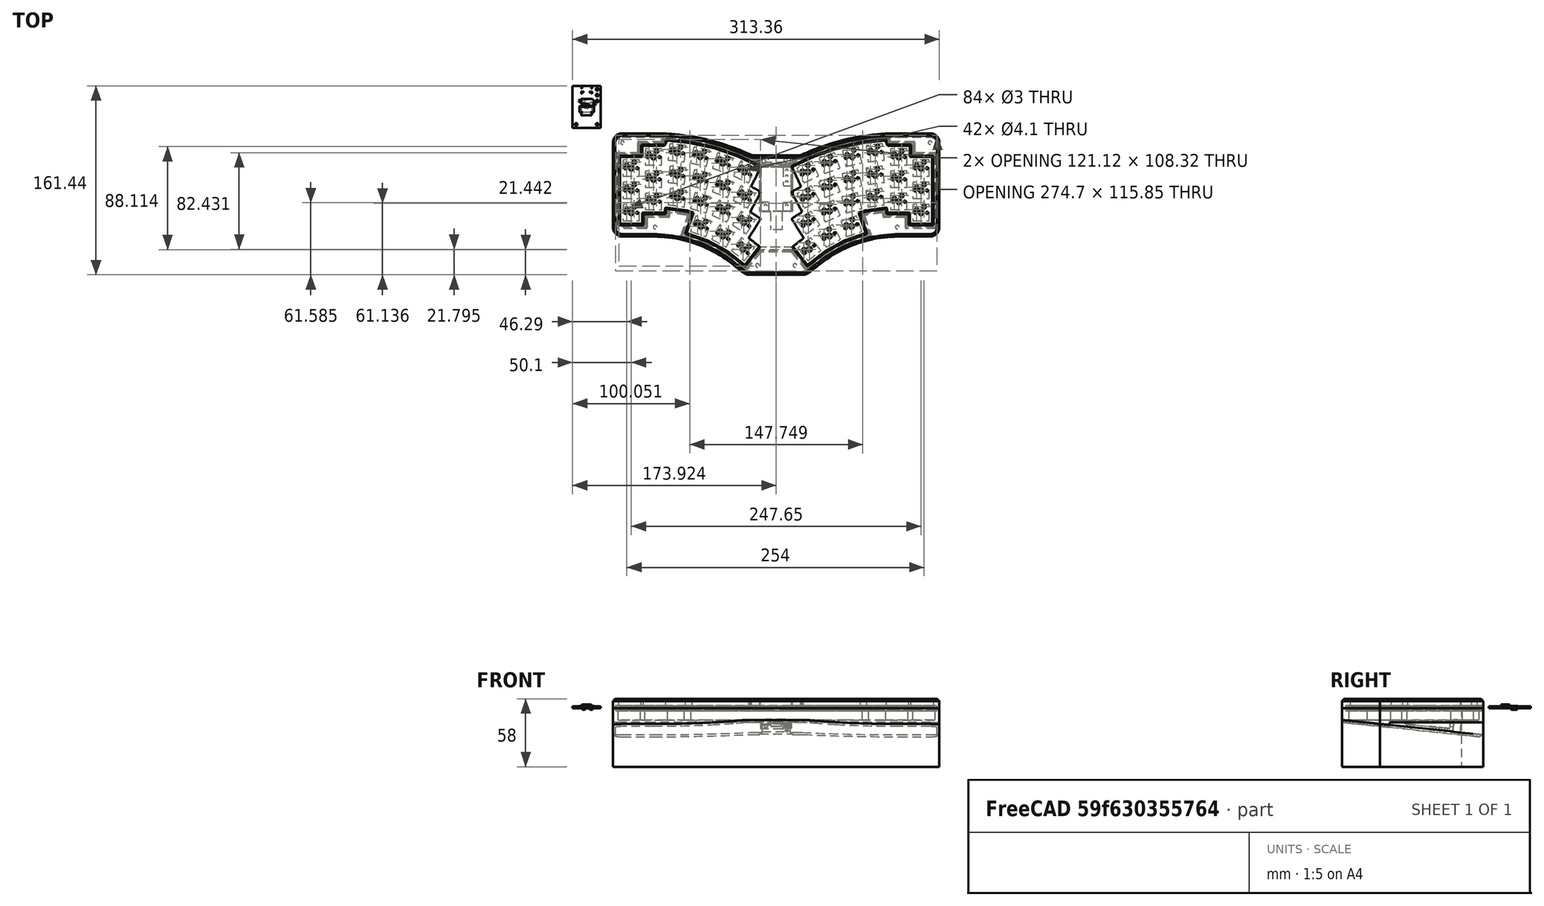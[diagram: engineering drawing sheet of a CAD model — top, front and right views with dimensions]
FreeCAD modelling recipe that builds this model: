
FCSTD DOCUMENT  (FreeCAD 0.21R33771 (Git))
Label: harmony-42-case
License: All rights reserved
LicenseURL: http://en.wikipedia.org/wiki/All_rights_reserved
objects: Part::Feature×116, App::Part×115, Sketcher::SketchObject×16, PartDesign::Pocket×11, PartDesign::Fillet×11, PartDesign::Pad×5, TechDraw::DrawViewBalloon×5, PartDesign::Body×3, PartDesign::Chamfer×3, PartDesign::Boolean×1, PartDesign::Hole×1, TechDraw::DrawSVGTemplate×1, TechDraw::DrawViewPart×1, TechDraw::DrawPage×1, App::DocumentObjectGroup×1
note: 198 computed .brp shape members not serialized (recipe doc carries the construction recipe); baked Part::Feature solids carry a one-line shape summary decoded from their .brp

FEATURE [Sketcher::SketchObject] Sketch
  FullyConstrained = false
  sketch-geometry (14):
    g0: BSplineCurve PolesCount=4 KnotsCount=2 Degree=3 IsPeriodic=0
    g1: BSplineCurve PolesCount=2 KnotsCount=2 Degree=1 IsPeriodic=0
    g2: BSplineCurve PolesCount=2 KnotsCount=2 Degree=1 IsPeriodic=0
    g3: BSplineCurve PolesCount=2 KnotsCount=2 Degree=1 IsPeriodic=0
    g4: BSplineCurve PolesCount=4 KnotsCount=2 Degree=3 IsPeriodic=0
    g5: BSplineCurve PolesCount=2 KnotsCount=2 Degree=1 IsPeriodic=0
    g6: BSplineCurve PolesCount=2 KnotsCount=2 Degree=1 IsPeriodic=0
    g7: BSplineCurve PolesCount=2 KnotsCount=2 Degree=1 IsPeriodic=0
    g8: BSplineCurve PolesCount=4 KnotsCount=2 Degree=3 IsPeriodic=0
    g9: BSplineCurve PolesCount=2 KnotsCount=2 Degree=1 IsPeriodic=0
    g10: BSplineCurve PolesCount=2 KnotsCount=2 Degree=1 IsPeriodic=0
    g11: BSplineCurve PolesCount=2 KnotsCount=2 Degree=1 IsPeriodic=0
    g12: BSplineCurve PolesCount=4 KnotsCount=2 Degree=3 IsPeriodic=0
    g13: BSplineCurve PolesCount=2 KnotsCount=2 Degree=1 IsPeriodic=0
  constraints (14):
    c: Coincident(g0,g1)
    c: Coincident(g1,g2)
    c: Coincident(g2,g3)
    c: Coincident(g3,g4)
    c: Coincident(g4,g5)
    c: Coincident(g5,g6)
    c: Coincident(g6,g7)
    c: Coincident(g7,g8)
    c: Coincident(g8,g9)
    c: Coincident(g9,g10)
    c: Coincident(g10,g11)
    c: Coincident(g11,g12)
    c: Coincident(g12,g13)
    c: Coincident(g13,g0)
FEATURE [PartDesign::Pad] Pad
  Direction = (0,0,1)
  Length = 12
  Length2 = 10
  Profile = -> Sketch
  ReferenceAxis = -> Sketch [N_Axis]
  Reversed = true
  Type = 0
FEATURE [Sketcher::SketchObject] Sketch001
  FullyConstrained = false
  Placement = pos=(0,0,0) rot=(0,0,1;3.14159rad)
  sketch-geometry (42):
    g0: BSplineCurve PolesCount=2 KnotsCount=2 Degree=1 IsPeriodic=0
    g1: BSplineCurve PolesCount=2 KnotsCount=2 Degree=1 IsPeriodic=0
    g2: BSplineCurve PolesCount=2 KnotsCount=2 Degree=1 IsPeriodic=0
    g3: BSplineCurve PolesCount=2 KnotsCount=2 Degree=1 IsPeriodic=0
    g4: BSplineCurve PolesCount=2 KnotsCount=2 Degree=1 IsPeriodic=0
    g5: BSplineCurve PolesCount=2 KnotsCount=2 Degree=1 IsPeriodic=0
    g6: BSplineCurve PolesCount=2 KnotsCount=2 Degree=1 IsPeriodic=0
    g7: BSplineCurve PolesCount=2 KnotsCount=2 Degree=1 IsPeriodic=0
    g8: BSplineCurve PolesCount=2 KnotsCount=2 Degree=1 IsPeriodic=0
    g9: BSplineCurve PolesCount=2 KnotsCount=2 Degree=1 IsPeriodic=0
    g10: BSplineCurve PolesCount=2 KnotsCount=2 Degree=1 IsPeriodic=0
    g11: BSplineCurve PolesCount=2 KnotsCount=2 Degree=1 IsPeriodic=0
    g12: BSplineCurve PolesCount=2 KnotsCount=2 Degree=1 IsPeriodic=0
    g13: BSplineCurve PolesCount=2 KnotsCount=2 Degree=1 IsPeriodic=0
    g14: BSplineCurve PolesCount=2 KnotsCount=2 Degree=1 IsPeriodic=0
    g15: BSplineCurve PolesCount=2 KnotsCount=2 Degree=1 IsPeriodic=0
    g16: BSplineCurve PolesCount=2 KnotsCount=2 Degree=1 IsPeriodic=0
    g17: BSplineCurve PolesCount=2 KnotsCount=2 Degree=1 IsPeriodic=0
    g18: BSplineCurve PolesCount=2 KnotsCount=2 Degree=1 IsPeriodic=0
    g19: BSplineCurve PolesCount=2 KnotsCount=2 Degree=1 IsPeriodic=0
    g20: BSplineCurve PolesCount=2 KnotsCount=2 Degree=1 IsPeriodic=0
    g21: BSplineCurve PolesCount=2 KnotsCount=2 Degree=1 IsPeriodic=0
    g22: BSplineCurve PolesCount=2 KnotsCount=2 Degree=1 IsPeriodic=0
    g23: BSplineCurve PolesCount=2 KnotsCount=2 Degree=1 IsPeriodic=0
    g24: BSplineCurve PolesCount=2 KnotsCount=2 Degree=1 IsPeriodic=0
    g25: BSplineCurve PolesCount=2 KnotsCount=2 Degree=1 IsPeriodic=0
    g26: BSplineCurve PolesCount=2 KnotsCount=2 Degree=1 IsPeriodic=0
    g27: BSplineCurve PolesCount=2 KnotsCount=2 Degree=1 IsPeriodic=0
    g28: BSplineCurve PolesCount=2 KnotsCount=2 Degree=1 IsPeriodic=0
    g29: BSplineCurve PolesCount=2 KnotsCount=2 Degree=1 IsPeriodic=0
    g30: BSplineCurve PolesCount=2 KnotsCount=2 Degree=1 IsPeriodic=0
    g31: BSplineCurve PolesCount=2 KnotsCount=2 Degree=1 IsPeriodic=0
    g32: BSplineCurve PolesCount=2 KnotsCount=2 Degree=1 IsPeriodic=0
    g33: BSplineCurve PolesCount=2 KnotsCount=2 Degree=1 IsPeriodic=0
    g34: BSplineCurve PolesCount=2 KnotsCount=2 Degree=1 IsPeriodic=0
    g35: BSplineCurve PolesCount=2 KnotsCount=2 Degree=1 IsPeriodic=0
    g36: BSplineCurve PolesCount=2 KnotsCount=2 Degree=1 IsPeriodic=0
    g37: BSplineCurve PolesCount=2 KnotsCount=2 Degree=1 IsPeriodic=0
    g38: BSplineCurve PolesCount=2 KnotsCount=2 Degree=1 IsPeriodic=0
    g39: BSplineCurve PolesCount=2 KnotsCount=2 Degree=1 IsPeriodic=0
    g40: BSplineCurve PolesCount=2 KnotsCount=2 Degree=1 IsPeriodic=0
    g41: BSplineCurve PolesCount=2 KnotsCount=2 Degree=1 IsPeriodic=0
  constraints (42):
    c: Coincident(g0,g1)
    c: Coincident(g1,g2)
    c: Coincident(g2,g3)
    c: Coincident(g3,g4)
    c: Coincident(g4,g5)
    c: Coincident(g5,g6)
    c: Coincident(g6,g7)
    c: Coincident(g7,g8)
    c: Coincident(g8,g9)
    c: Coincident(g9,g10)
    c: Coincident(g10,g11)
    c: Coincident(g11,g12)
    c: Coincident(g12,g13)
    c: Coincident(g13,g14)
    c: Coincident(g14,g15)
    c: Coincident(g15,g16)
    c: Coincident(g16,g17)
    c: Coincident(g17,g18)
    c: Coincident(g18,g19)
    c: Coincident(g19,g20)
    c: Coincident(g20,g21)
    c: Coincident(g21,g22)
    c: Coincident(g22,g23)
    c: Coincident(g23,g24)
    c: Coincident(g24,g25)
    c: Coincident(g25,g26)
    c: Coincident(g26,g27)
    c: Coincident(g27,g28)
    c: Coincident(g28,g29)
    c: Coincident(g29,g30)
    c: Coincident(g30,g31)
    c: Coincident(g31,g32)
    c: Coincident(g32,g33)
    c: Coincident(g33,g34)
    c: Coincident(g34,g35)
    c: Coincident(g35,g36)
    c: Coincident(g36,g37)
    c: Coincident(g37,g38)
    c: Coincident(g38,g39)
    c: Coincident(g39,g40)
    c: Coincident(g40,g41)
    c: Coincident(g41,g0)
FEATURE [PartDesign::Pocket] Pocket
  BaseFeature = -> Pad
  Direction = (0,0,-1)
  Length = 10
  Length2 = 5
  Profile = -> Sketch001
  ReferenceAxis = -> Sketch001 [N_Axis]
  Type = 0
FEATURE [Sketcher::SketchObject] Sketch002
  FullyConstrained = false
  Placement = pos=(0,0,0) rot=(0,0,1;3.14159rad)
  sketch-geometry (42):
    g0: BSplineCurve PolesCount=2 KnotsCount=2 Degree=1 IsPeriodic=0
    g1: BSplineCurve PolesCount=2 KnotsCount=2 Degree=1 IsPeriodic=0
    g2: BSplineCurve PolesCount=2 KnotsCount=2 Degree=1 IsPeriodic=0
    g3: BSplineCurve PolesCount=2 KnotsCount=2 Degree=1 IsPeriodic=0
    g4: BSplineCurve PolesCount=2 KnotsCount=2 Degree=1 IsPeriodic=0
    g5: BSplineCurve PolesCount=2 KnotsCount=2 Degree=1 IsPeriodic=0
    g6: BSplineCurve PolesCount=2 KnotsCount=2 Degree=1 IsPeriodic=0
    g7: BSplineCurve PolesCount=2 KnotsCount=2 Degree=1 IsPeriodic=0
    g8: BSplineCurve PolesCount=2 KnotsCount=2 Degree=1 IsPeriodic=0
    g9: BSplineCurve PolesCount=2 KnotsCount=2 Degree=1 IsPeriodic=0
    g10: BSplineCurve PolesCount=2 KnotsCount=2 Degree=1 IsPeriodic=0
    g11: BSplineCurve PolesCount=2 KnotsCount=2 Degree=1 IsPeriodic=0
    g12: BSplineCurve PolesCount=2 KnotsCount=2 Degree=1 IsPeriodic=0
    g13: BSplineCurve PolesCount=2 KnotsCount=2 Degree=1 IsPeriodic=0
    g14: BSplineCurve PolesCount=2 KnotsCount=2 Degree=1 IsPeriodic=0
    g15: BSplineCurve PolesCount=2 KnotsCount=2 Degree=1 IsPeriodic=0
    g16: BSplineCurve PolesCount=2 KnotsCount=2 Degree=1 IsPeriodic=0
    g17: BSplineCurve PolesCount=2 KnotsCount=2 Degree=1 IsPeriodic=0
    g18: BSplineCurve PolesCount=2 KnotsCount=2 Degree=1 IsPeriodic=0
    g19: BSplineCurve PolesCount=2 KnotsCount=2 Degree=1 IsPeriodic=0
    g20: BSplineCurve PolesCount=2 KnotsCount=2 Degree=1 IsPeriodic=0
    g21: BSplineCurve PolesCount=2 KnotsCount=2 Degree=1 IsPeriodic=0
    g22: BSplineCurve PolesCount=2 KnotsCount=2 Degree=1 IsPeriodic=0
    g23: BSplineCurve PolesCount=2 KnotsCount=2 Degree=1 IsPeriodic=0
    g24: BSplineCurve PolesCount=2 KnotsCount=2 Degree=1 IsPeriodic=0
    g25: BSplineCurve PolesCount=2 KnotsCount=2 Degree=1 IsPeriodic=0
    g26: BSplineCurve PolesCount=2 KnotsCount=2 Degree=1 IsPeriodic=0
    g27: BSplineCurve PolesCount=2 KnotsCount=2 Degree=1 IsPeriodic=0
    g28: BSplineCurve PolesCount=2 KnotsCount=2 Degree=1 IsPeriodic=0
    g29: BSplineCurve PolesCount=2 KnotsCount=2 Degree=1 IsPeriodic=0
    g30: BSplineCurve PolesCount=2 KnotsCount=2 Degree=1 IsPeriodic=0
    g31: BSplineCurve PolesCount=2 KnotsCount=2 Degree=1 IsPeriodic=0
    g32: BSplineCurve PolesCount=2 KnotsCount=2 Degree=1 IsPeriodic=0
    g33: BSplineCurve PolesCount=2 KnotsCount=2 Degree=1 IsPeriodic=0
    g34: BSplineCurve PolesCount=2 KnotsCount=2 Degree=1 IsPeriodic=0
    g35: BSplineCurve PolesCount=2 KnotsCount=2 Degree=1 IsPeriodic=0
    g36: BSplineCurve PolesCount=2 KnotsCount=2 Degree=1 IsPeriodic=0
    g37: BSplineCurve PolesCount=2 KnotsCount=2 Degree=1 IsPeriodic=0
    g38: BSplineCurve PolesCount=2 KnotsCount=2 Degree=1 IsPeriodic=0
    g39: BSplineCurve PolesCount=2 KnotsCount=2 Degree=1 IsPeriodic=0
    g40: BSplineCurve PolesCount=2 KnotsCount=2 Degree=1 IsPeriodic=0
    g41: BSplineCurve PolesCount=2 KnotsCount=2 Degree=1 IsPeriodic=0
  constraints (42):
    c: Coincident(g0,g1)
    c: Coincident(g1,g2)
    c: Coincident(g2,g3)
    c: Coincident(g3,g4)
    c: Coincident(g4,g5)
    c: Coincident(g5,g6)
    c: Coincident(g6,g7)
    c: Coincident(g7,g8)
    c: Coincident(g8,g9)
    c: Coincident(g9,g10)
    c: Coincident(g10,g11)
    c: Coincident(g11,g12)
    c: Coincident(g12,g13)
    c: Coincident(g13,g14)
    c: Coincident(g14,g15)
    c: Coincident(g15,g16)
    c: Coincident(g16,g17)
    c: Coincident(g17,g18)
    c: Coincident(g18,g19)
    c: Coincident(g19,g20)
    c: Coincident(g20,g21)
    c: Coincident(g21,g22)
    c: Coincident(g22,g23)
    c: Coincident(g23,g24)
    c: Coincident(g24,g25)
    c: Coincident(g25,g26)
    c: Coincident(g26,g27)
    c: Coincident(g27,g28)
    c: Coincident(g28,g29)
    c: Coincident(g29,g30)
    c: Coincident(g30,g31)
    c: Coincident(g31,g32)
    c: Coincident(g32,g33)
    c: Coincident(g33,g34)
    c: Coincident(g34,g35)
    c: Coincident(g35,g36)
    c: Coincident(g36,g37)
    c: Coincident(g37,g38)
    c: Coincident(g38,g39)
    c: Coincident(g39,g40)
    c: Coincident(g40,g41)
    c: Coincident(g41,g0)
FEATURE [PartDesign::Pocket] Pocket001  label="Pocket001 - Gasket"
  BaseFeature = -> Pocket
  Direction = (0,0,-1)
  Length = 2.25
  Length2 = 5
  Profile = -> Sketch002
  ReferenceAxis = -> Sketch002 [N_Axis]
  Type = 0
  expr: Length = 1.5 mm / 2 + 2 mm - 0.5 mm
FEATURE [Sketcher::SketchObject] Sketch003
  FullyConstrained = false
  sketch-geometry (14):
    g0: BSplineCurve PolesCount=4 KnotsCount=2 Degree=3 IsPeriodic=0
    g1: BSplineCurve PolesCount=2 KnotsCount=2 Degree=1 IsPeriodic=0
    g2: BSplineCurve PolesCount=2 KnotsCount=2 Degree=1 IsPeriodic=0
    g3: BSplineCurve PolesCount=2 KnotsCount=2 Degree=1 IsPeriodic=0
    g4: BSplineCurve PolesCount=4 KnotsCount=2 Degree=3 IsPeriodic=0
    g5: BSplineCurve PolesCount=2 KnotsCount=2 Degree=1 IsPeriodic=0
    g6: BSplineCurve PolesCount=2 KnotsCount=2 Degree=1 IsPeriodic=0
    g7: BSplineCurve PolesCount=2 KnotsCount=2 Degree=1 IsPeriodic=0
    g8: BSplineCurve PolesCount=4 KnotsCount=2 Degree=3 IsPeriodic=0
    g9: BSplineCurve PolesCount=2 KnotsCount=2 Degree=1 IsPeriodic=0
    g10: BSplineCurve PolesCount=2 KnotsCount=2 Degree=1 IsPeriodic=0
    g11: BSplineCurve PolesCount=2 KnotsCount=2 Degree=1 IsPeriodic=0
    g12: BSplineCurve PolesCount=4 KnotsCount=2 Degree=3 IsPeriodic=0
    g13: BSplineCurve PolesCount=2 KnotsCount=2 Degree=1 IsPeriodic=0
  constraints (14):
    c: Coincident(g0,g1)
    c: Coincident(g1,g2)
    c: Coincident(g2,g3)
    c: Coincident(g3,g4)
    c: Coincident(g4,g5)
    c: Coincident(g5,g6)
    c: Coincident(g6,g7)
    c: Coincident(g7,g8)
    c: Coincident(g8,g9)
    c: Coincident(g9,g10)
    c: Coincident(g10,g11)
    c: Coincident(g11,g12)
    c: Coincident(g12,g13)
    c: Coincident(g13,g0)
FEATURE [PartDesign::Pad] Pad001
  Direction = (0,0,1)
  Length = 8
  Length2 = 10
  Profile = -> Sketch003
  ReferenceAxis = -> Sketch003 [N_Axis]
  Type = 0
FEATURE [Sketcher::SketchObject] Sketch004
  FullyConstrained = false
  sketch-geometry (52):
    g0: BSplineCurve PolesCount=2 KnotsCount=2 Degree=1 IsPeriodic=0
    g1: BSplineCurve PolesCount=2 KnotsCount=2 Degree=1 IsPeriodic=0
    g2: BSplineCurve PolesCount=2 KnotsCount=2 Degree=1 IsPeriodic=0
    g3: BSplineCurve PolesCount=2 KnotsCount=2 Degree=1 IsPeriodic=0
    g4: BSplineCurve PolesCount=2 KnotsCount=2 Degree=1 IsPeriodic=0
    g5: BSplineCurve PolesCount=2 KnotsCount=2 Degree=1 IsPeriodic=0
    g6: BSplineCurve PolesCount=2 KnotsCount=2 Degree=1 IsPeriodic=0
    g7: BSplineCurve PolesCount=2 KnotsCount=2 Degree=1 IsPeriodic=0
    g8: BSplineCurve PolesCount=2 KnotsCount=2 Degree=1 IsPeriodic=0
    g9: BSplineCurve PolesCount=2 KnotsCount=2 Degree=1 IsPeriodic=0
    g10: BSplineCurve PolesCount=2 KnotsCount=2 Degree=1 IsPeriodic=0
    g11: BSplineCurve PolesCount=2 KnotsCount=2 Degree=1 IsPeriodic=0
    g12: BSplineCurve PolesCount=2 KnotsCount=2 Degree=1 IsPeriodic=0
    g13: BSplineCurve PolesCount=2 KnotsCount=2 Degree=1 IsPeriodic=0
    g14: BSplineCurve PolesCount=2 KnotsCount=2 Degree=1 IsPeriodic=0
    g15: BSplineCurve PolesCount=2 KnotsCount=2 Degree=1 IsPeriodic=0
    g16: BSplineCurve PolesCount=2 KnotsCount=2 Degree=1 IsPeriodic=0
    g17: BSplineCurve PolesCount=2 KnotsCount=2 Degree=1 IsPeriodic=0
    g18: BSplineCurve PolesCount=2 KnotsCount=2 Degree=1 IsPeriodic=0
    g19: BSplineCurve PolesCount=2 KnotsCount=2 Degree=1 IsPeriodic=0
    g20: BSplineCurve PolesCount=2 KnotsCount=2 Degree=1 IsPeriodic=0
    g21: BSplineCurve PolesCount=2 KnotsCount=2 Degree=1 IsPeriodic=0
    g22: BSplineCurve PolesCount=2 KnotsCount=2 Degree=1 IsPeriodic=0
    g23: BSplineCurve PolesCount=2 KnotsCount=2 Degree=1 IsPeriodic=0
    g24: BSplineCurve PolesCount=2 KnotsCount=2 Degree=1 IsPeriodic=0
    g25: BSplineCurve PolesCount=2 KnotsCount=2 Degree=1 IsPeriodic=0
    g26: BSplineCurve PolesCount=2 KnotsCount=2 Degree=1 IsPeriodic=0
    g27: BSplineCurve PolesCount=2 KnotsCount=2 Degree=1 IsPeriodic=0
    g28: BSplineCurve PolesCount=2 KnotsCount=2 Degree=1 IsPeriodic=0
    g29: BSplineCurve PolesCount=2 KnotsCount=2 Degree=1 IsPeriodic=0
    g30: BSplineCurve PolesCount=2 KnotsCount=2 Degree=1 IsPeriodic=0
    g31: BSplineCurve PolesCount=2 KnotsCount=2 Degree=1 IsPeriodic=0
    g32: BSplineCurve PolesCount=2 KnotsCount=2 Degree=1 IsPeriodic=0
    g33: BSplineCurve PolesCount=2 KnotsCount=2 Degree=1 IsPeriodic=0
    g34: BSplineCurve PolesCount=2 KnotsCount=2 Degree=1 IsPeriodic=0
    g35: BSplineCurve PolesCount=2 KnotsCount=2 Degree=1 IsPeriodic=0
    g36: BSplineCurve PolesCount=2 KnotsCount=2 Degree=1 IsPeriodic=0
    g37: BSplineCurve PolesCount=2 KnotsCount=2 Degree=1 IsPeriodic=0
    g38: BSplineCurve PolesCount=2 KnotsCount=2 Degree=1 IsPeriodic=0
    g39: BSplineCurve PolesCount=2 KnotsCount=2 Degree=1 IsPeriodic=0
    g40: BSplineCurve PolesCount=2 KnotsCount=2 Degree=1 IsPeriodic=0
    g41: BSplineCurve PolesCount=2 KnotsCount=2 Degree=1 IsPeriodic=0
    g42: BSplineCurve PolesCount=2 KnotsCount=2 Degree=1 IsPeriodic=0
    g43: BSplineCurve PolesCount=2 KnotsCount=2 Degree=1 IsPeriodic=0
    g44: BSplineCurve PolesCount=2 KnotsCount=2 Degree=1 IsPeriodic=0
    g45: BSplineCurve PolesCount=2 KnotsCount=2 Degree=1 IsPeriodic=0
    g46: BSplineCurve PolesCount=2 KnotsCount=2 Degree=1 IsPeriodic=0
    g47: BSplineCurve PolesCount=2 KnotsCount=2 Degree=1 IsPeriodic=0
    g48: BSplineCurve PolesCount=2 KnotsCount=2 Degree=1 IsPeriodic=0
    g49: BSplineCurve PolesCount=2 KnotsCount=2 Degree=1 IsPeriodic=0
    g50: BSplineCurve PolesCount=2 KnotsCount=2 Degree=1 IsPeriodic=0
    g51: BSplineCurve PolesCount=2 KnotsCount=2 Degree=1 IsPeriodic=0
  constraints (52):
    c: Coincident(g0,g1)
    c: Coincident(g1,g2)
    c: Coincident(g2,g3)
    c: Coincident(g3,g4)
    c: Coincident(g4,g5)
    c: Coincident(g5,g6)
    c: Coincident(g6,g7)
    c: Coincident(g7,g8)
    c: Coincident(g8,g9)
    c: Coincident(g9,g10)
    c: Coincident(g10,g11)
    c: Coincident(g11,g12)
    c: Coincident(g12,g13)
    c: Coincident(g13,g14)
    c: Coincident(g14,g15)
    c: Coincident(g15,g16)
    c: Coincident(g16,g17)
    c: Coincident(g17,g18)
    c: Coincident(g18,g19)
    c: Coincident(g19,g20)
    c: Coincident(g20,g21)
    c: Coincident(g21,g22)
    c: Coincident(g22,g23)
    c: Coincident(g23,g24)
    c: Coincident(g24,g25)
    c: Coincident(g25,g0)
    c: Coincident(g26,g27)
    c: Coincident(g27,g28)
    c: Coincident(g28,g29)
    c: Coincident(g29,g30)
    c: Coincident(g30,g31)
    c: Coincident(g31,g32)
    c: Coincident(g32,g33)
    c: Coincident(g33,g34)
    c: Coincident(g34,g35)
    c: Coincident(g35,g36)
    c: Coincident(g36,g37)
    c: Coincident(g37,g38)
    c: Coincident(g38,g39)
    c: Coincident(g39,g40)
    c: Coincident(g40,g41)
    c: Coincident(g41,g42)
    c: Coincident(g42,g43)
    c: Coincident(g43,g44)
    c: Coincident(g44,g45)
    c: Coincident(g45,g46)
    c: Coincident(g46,g47)
    c: Coincident(g47,g48)
    c: Coincident(g48,g49)
    c: Coincident(g49,g50)
    c: Coincident(g50,g51)
    c: Coincident(g51,g26)
FEATURE [PartDesign::Pocket] Pocket002
  BaseFeature = -> Pad001
  Direction = (0,0,-1)
  Length = 5
  Length2 = 5
  Profile = -> Sketch004
  ReferenceAxis = -> Sketch004 [N_Axis]
  Reversed = true
  Type = 1
FEATURE [Sketcher::SketchObject] Sketch005
  FullyConstrained = false
  Placement = pos=(0,0,0) rot=(0,0,1;3.14159rad)
  sketch-geometry (42):
    g0: BSplineCurve PolesCount=2 KnotsCount=2 Degree=1 IsPeriodic=0
    g1: BSplineCurve PolesCount=2 KnotsCount=2 Degree=1 IsPeriodic=0
    g2: BSplineCurve PolesCount=2 KnotsCount=2 Degree=1 IsPeriodic=0
    g3: BSplineCurve PolesCount=2 KnotsCount=2 Degree=1 IsPeriodic=0
    g4: BSplineCurve PolesCount=2 KnotsCount=2 Degree=1 IsPeriodic=0
    g5: BSplineCurve PolesCount=2 KnotsCount=2 Degree=1 IsPeriodic=0
    g6: BSplineCurve PolesCount=2 KnotsCount=2 Degree=1 IsPeriodic=0
    g7: BSplineCurve PolesCount=2 KnotsCount=2 Degree=1 IsPeriodic=0
    g8: BSplineCurve PolesCount=2 KnotsCount=2 Degree=1 IsPeriodic=0
    g9: BSplineCurve PolesCount=2 KnotsCount=2 Degree=1 IsPeriodic=0
    g10: BSplineCurve PolesCount=2 KnotsCount=2 Degree=1 IsPeriodic=0
    g11: BSplineCurve PolesCount=2 KnotsCount=2 Degree=1 IsPeriodic=0
    g12: BSplineCurve PolesCount=2 KnotsCount=2 Degree=1 IsPeriodic=0
    g13: BSplineCurve PolesCount=2 KnotsCount=2 Degree=1 IsPeriodic=0
    g14: BSplineCurve PolesCount=2 KnotsCount=2 Degree=1 IsPeriodic=0
    g15: BSplineCurve PolesCount=2 KnotsCount=2 Degree=1 IsPeriodic=0
    g16: BSplineCurve PolesCount=2 KnotsCount=2 Degree=1 IsPeriodic=0
    g17: BSplineCurve PolesCount=2 KnotsCount=2 Degree=1 IsPeriodic=0
    g18: BSplineCurve PolesCount=2 KnotsCount=2 Degree=1 IsPeriodic=0
    g19: BSplineCurve PolesCount=2 KnotsCount=2 Degree=1 IsPeriodic=0
    g20: BSplineCurve PolesCount=2 KnotsCount=2 Degree=1 IsPeriodic=0
    g21: BSplineCurve PolesCount=2 KnotsCount=2 Degree=1 IsPeriodic=0
    g22: BSplineCurve PolesCount=2 KnotsCount=2 Degree=1 IsPeriodic=0
    g23: BSplineCurve PolesCount=2 KnotsCount=2 Degree=1 IsPeriodic=0
    g24: BSplineCurve PolesCount=2 KnotsCount=2 Degree=1 IsPeriodic=0
    g25: BSplineCurve PolesCount=2 KnotsCount=2 Degree=1 IsPeriodic=0
    g26: BSplineCurve PolesCount=2 KnotsCount=2 Degree=1 IsPeriodic=0
    g27: BSplineCurve PolesCount=2 KnotsCount=2 Degree=1 IsPeriodic=0
    g28: BSplineCurve PolesCount=2 KnotsCount=2 Degree=1 IsPeriodic=0
    g29: BSplineCurve PolesCount=2 KnotsCount=2 Degree=1 IsPeriodic=0
    g30: BSplineCurve PolesCount=2 KnotsCount=2 Degree=1 IsPeriodic=0
    g31: BSplineCurve PolesCount=2 KnotsCount=2 Degree=1 IsPeriodic=0
    g32: BSplineCurve PolesCount=2 KnotsCount=2 Degree=1 IsPeriodic=0
    g33: BSplineCurve PolesCount=2 KnotsCount=2 Degree=1 IsPeriodic=0
    g34: BSplineCurve PolesCount=2 KnotsCount=2 Degree=1 IsPeriodic=0
    g35: BSplineCurve PolesCount=2 KnotsCount=2 Degree=1 IsPeriodic=0
    g36: BSplineCurve PolesCount=2 KnotsCount=2 Degree=1 IsPeriodic=0
    g37: BSplineCurve PolesCount=2 KnotsCount=2 Degree=1 IsPeriodic=0
    g38: BSplineCurve PolesCount=2 KnotsCount=2 Degree=1 IsPeriodic=0
    g39: BSplineCurve PolesCount=2 KnotsCount=2 Degree=1 IsPeriodic=0
    g40: BSplineCurve PolesCount=2 KnotsCount=2 Degree=1 IsPeriodic=0
    g41: BSplineCurve PolesCount=2 KnotsCount=2 Degree=1 IsPeriodic=0
  constraints (42):
    c: Coincident(g0,g1)
    c: Coincident(g1,g2)
    c: Coincident(g2,g3)
    c: Coincident(g3,g4)
    c: Coincident(g4,g5)
    c: Coincident(g5,g6)
    c: Coincident(g6,g7)
    c: Coincident(g7,g8)
    c: Coincident(g8,g9)
    c: Coincident(g9,g10)
    c: Coincident(g10,g11)
    c: Coincident(g11,g12)
    c: Coincident(g12,g13)
    c: Coincident(g13,g14)
    c: Coincident(g14,g15)
    c: Coincident(g15,g16)
    c: Coincident(g16,g17)
    c: Coincident(g17,g18)
    c: Coincident(g18,g19)
    c: Coincident(g19,g20)
    c: Coincident(g20,g21)
    c: Coincident(g21,g22)
    c: Coincident(g22,g23)
    c: Coincident(g23,g24)
    c: Coincident(g24,g25)
    c: Coincident(g25,g26)
    c: Coincident(g26,g27)
    c: Coincident(g27,g28)
    c: Coincident(g28,g29)
    c: Coincident(g29,g30)
    c: Coincident(g30,g31)
    c: Coincident(g31,g32)
    c: Coincident(g32,g33)
    c: Coincident(g33,g34)
    c: Coincident(g34,g35)
    c: Coincident(g35,g36)
    c: Coincident(g36,g37)
    c: Coincident(g37,g38)
    c: Coincident(g38,g39)
    c: Coincident(g39,g40)
    c: Coincident(g40,g41)
    c: Coincident(g41,g0)
FEATURE [PartDesign::Pocket] Pocket003  label="Pocket003 - Gasket"
  BaseFeature = -> Pocket002
  Direction = (0,0,-1)
  Length = 2.25
  Length2 = 5
  Profile = -> Sketch005
  ReferenceAxis = -> Sketch005 [N_Axis]
  Reversed = true
  Type = 0
  expr: Length = 1.5 mm / 2 + 2 mm - 0.5 mm
FEATURE [Sketcher::SketchObject] Sketch006
  FullyConstrained = false
  sketch-geometry (14):
    g0: BSplineCurve PolesCount=4 KnotsCount=2 Degree=3 IsPeriodic=0
    g1: BSplineCurve PolesCount=2 KnotsCount=2 Degree=1 IsPeriodic=0
    g2: BSplineCurve PolesCount=2 KnotsCount=2 Degree=1 IsPeriodic=0
    g3: BSplineCurve PolesCount=2 KnotsCount=2 Degree=1 IsPeriodic=0
    g4: BSplineCurve PolesCount=4 KnotsCount=2 Degree=3 IsPeriodic=0
    g5: BSplineCurve PolesCount=2 KnotsCount=2 Degree=1 IsPeriodic=0
    g6: BSplineCurve PolesCount=2 KnotsCount=2 Degree=1 IsPeriodic=0
    g7: BSplineCurve PolesCount=2 KnotsCount=2 Degree=1 IsPeriodic=0
    g8: BSplineCurve PolesCount=4 KnotsCount=2 Degree=3 IsPeriodic=0
    g9: BSplineCurve PolesCount=2 KnotsCount=2 Degree=1 IsPeriodic=0
    g10: BSplineCurve PolesCount=2 KnotsCount=2 Degree=1 IsPeriodic=0
    g11: BSplineCurve PolesCount=2 KnotsCount=2 Degree=1 IsPeriodic=0
    g12: BSplineCurve PolesCount=4 KnotsCount=2 Degree=3 IsPeriodic=0
    g13: BSplineCurve PolesCount=2 KnotsCount=2 Degree=1 IsPeriodic=0
  constraints (14):
    c: Coincident(g0,g1)
    c: Coincident(g1,g2)
    c: Coincident(g2,g3)
    c: Coincident(g3,g4)
    c: Coincident(g4,g5)
    c: Coincident(g5,g6)
    c: Coincident(g6,g7)
    c: Coincident(g7,g8)
    c: Coincident(g8,g9)
    c: Coincident(g9,g10)
    c: Coincident(g10,g11)
    c: Coincident(g11,g12)
    c: Coincident(g12,g13)
    c: Coincident(g13,g0)
FEATURE [PartDesign::Pad] Pad003
  Direction = (0,0,1)
  Length = 50
  Length2 = 10
  Profile = -> Sketch006
  ReferenceAxis = -> Sketch006 [N_Axis]
  Reversed = true
  Type = 0
FEATURE [PartDesign::Fillet] Fillet
  Base = -> Pocket001 [Edge79,Edge84,Edge77,Edge5,Edge1,Edge8,Edge82,Edge76]
  BaseFeature = -> Pocket001
  Radius = 8
  SupportTransform = false
  UseAllEdges = false
FEATURE [PartDesign::Pad] Pad004
  BaseFeature = -> Fillet
  Direction = (0,-0.105104,-1)
  Length = 20
  Length2 = 10
  Profile = -> Fillet [Face5]
  Type = 0
  UseCustomVector = true
  expr: .Direction.y = -0.10510423526
FEATURE [PartDesign::Fillet] Fillet001
  Base = -> Pad004
  BaseFeature = -> Pad004
  Radius = 1
  SupportTransform = false
  UseAllEdges = false
FEATURE [PartDesign::Fillet] Fillet002
  Base = -> Pad003 [Edge20,Edge17,Edge29,Edge32,Edge8,Edge38,Edge1,Edge5]
  BaseFeature = -> Pad003
  Radius = 8
  SupportTransform = false
  UseAllEdges = false
FEATURE [PartDesign::Body] Body002  label="Body"
  Group = -> [Sketch006,Pad003,Fillet002]
  Origin = -> Origin002
  Tip = -> Fillet002
FEATURE [PartDesign::Boolean] Boolean
  BaseFeature = -> Fillet001
  Group = -> [Body002]
  Type = 2
FEATURE [Sketcher::SketchObject] Sketch007
  ExternalGeometry = -> [Boolean]
  FullyConstrained = true
  MapMode = 5
  Placement = pos=(301.359,0,0) rot=(0.57735,0.57735,0.57735;2.0944rad)
  Support = -> [Boolean]
  sketch-geometry (4):
    g0: LineSegment StartX=-143.442 StartY=-12 StartZ=0 EndX=-23.896 EndY=-24.5648 EndZ=0
    g1: LineSegment StartX=-23.896 StartY=-24.5648 StartZ=0 EndX=-24.6775 EndY=-32 EndZ=0
    g2: LineSegment StartX=-24.6775 StartY=-32 StartZ=0 EndX=-143.442 EndY=-32 EndZ=0
    g3: LineSegment StartX=-143.442 StartY=-32 StartZ=0 EndX=-143.442 EndY=-12 EndZ=0
  constraints (10):
    c: Coincident(g0,g-3)
    c: PointOnObject(g0,g-4)
    c: Perpendicular(g-4,g0)
    c: Coincident(g1,g0)
    c: Coincident(g1,g-4)
    c: Coincident(g2,g1)
    c: Horizontal(g2)
    c: Coincident(g3,g2)
    c: Coincident(g3,g0)
    c: Vertical(g3)
FEATURE [PartDesign::Pocket] Pocket004
  BaseFeature = -> Boolean
  Direction = (-1,0,0)
  Length = 5
  Length2 = 5
  Profile = -> Sketch007
  ReferenceAxis = -> Sketch007 [N_Axis]
  Type = 1
FEATURE [PartDesign::Chamfer] Chamfer
  Angle = 45
  Base = -> Pocket004 [Edge203]
  BaseFeature = -> Pocket004
  ChamferType = 0
  FlipDirection = false
  Size = 2
  Size2 = 1
  SupportTransform = false
  UseAllEdges = false
FEATURE [PartDesign::Fillet] Fillet003
  Base = -> Pocket003 [Edge131,Edge136,Edge129,Edge5,Edge1,Edge8,Edge128,Edge134]
  BaseFeature = -> Pocket003
  Radius = 8
  SupportTransform = false
  UseAllEdges = false
FEATURE [PartDesign::Chamfer] Chamfer001
  Angle = 45
  Base = -> Fillet003 [Edge87]
  BaseFeature = -> Fillet003
  ChamferType = 0
  FlipDirection = false
  Size = 2
  Size2 = 4
  SupportTransform = false
  UseAllEdges = false
FEATURE [PartDesign::Fillet] Fillet004
  Base = -> Chamfer001 [Edge232,Edge234,Edge236,Edge238,Edge240,Edge242,Edge244,Edge248,Edge246,Edge250,Edge252,Edge254,Edge256,Edge258,Edge260,Edge262,Edge264,Edge266,Edge268,Edge188,Edge187,Edge190,Edge192,Edge194,Edge196,Edge200,Edge198,Edge202,Edge204,Edge206,Edge208,Edge210,Edge212,Edge214,Edge216,Edge220,Edge222,Edge224,Edge226,Edge228,+2 more]
  BaseFeature = -> Chamfer001
  Radius = 1
  SupportTransform = false
  UseAllEdges = false
FEATURE [PartDesign::Fillet] Fillet005
  Base = -> Fillet004 [Edge480,Edge478,Edge476,Edge474,Edge472,Edge482,Edge484,Edge486,Edge488,Edge490,Edge492,Edge494,Edge496,Edge498,Edge500,Edge502,Edge504,Edge506,Edge508,Edge510,Edge512,Edge514,Edge516,Edge469,Edge467,Edge470,Edge415,Edge417,Edge419,Edge421,Edge423,Edge425,Edge427,Edge431,Edge433,Edge435,Edge437,Edge439,Edge441,Edge443,+12 more]
  BaseFeature = -> Fillet004
  Radius = 1
  SupportTransform = false
  UseAllEdges = false
FEATURE [PartDesign::Fillet] Fillet006
  Base = -> Chamfer [Edge196,Edge198,Edge200,Edge194,Edge192,Edge190,Edge202,Edge204,Edge208,Edge206,Edge210,Edge212,Edge214,Edge216,Edge218,Edge222,Edge220,Edge224,Edge226,Edge228,Edge230,Edge232,Edge234,Edge236,Edge238,Edge240,Edge242,Edge244,Edge246,Edge248,Edge250,Edge252,Edge254,Edge256,Edge258,Edge260,Edge262,Edge264,Edge184,Edge183,+2 more]
  BaseFeature = -> Chamfer
  Radius = 1
  SupportTransform = false
  UseAllEdges = false
FEATURE [PartDesign::Fillet] Fillet007
  Base = -> Fillet006 [Edge427,Edge429,Edge425,Edge423,Edge421,Edge431,Edge433,Edge435,Edge437,Edge439,Edge441,Edge443,Edge445,Edge447,Edge449,Edge451,Edge453,Edge455,Edge457,Edge459,Edge461,Edge463,Edge465,Edge467,Edge469,Edge471,Edge473,Edge475,Edge477,Edge479,Edge481,Edge483,Edge485,Edge487,Edge489,Edge491,Edge493,Edge411,Edge413,Edge417,+2 more]
  BaseFeature = -> Fillet006
  Radius = 1
  SupportTransform = false
  UseAllEdges = false
FEATURE [Sketcher::SketchObject] Sketch008
  AttachmentOffset = pos=(0,0,161.925) rot=(0,0,1;0rad)
  ExternalGeometry = -> [Fillet007]
  FullyConstrained = true
  MapMode = 5
  Placement = pos=(161.925,-3.6e-14,3.6e-14) rot=(0.57735,0.57735,0.57735;2.0944rad)
  Support = -> [YZ_Plane]
  expr: .AttachmentOffset.Base.z = 149.925 mm + 24 mm / 2
  expr: Constraints[8] = 36 mm + 2 mm
  sketch-geometry (6):
    g0: LineSegment StartX=-102.836 StartY=-16.2679 StartZ=0 EndX=-31.845 EndY=-23.7293 EndZ=0
    g1: LineSegment StartX=-50.7153 StartY=-10 StartZ=0 EndX=-51.9363 EndY=-21.6176 EndZ=0
    g2: LineSegment StartX=-51.5182 StartY=-17.6395 StartZ=0 EndX=-89.31 EndY=-13.6675 EndZ=0
    g3: LineSegment StartX=-89.31 StartY=-13.6675 StartZ=0 EndX=-88.9246 EndY=-10 EndZ=0
    g4: LineSegment StartX=-88.9246 StartY=-10 StartZ=0 EndX=-50.7153 EndY=-10 EndZ=0
    g5: LineSegment StartX=-50.7153 StartY=-10 StartZ=0 EndX=-51.5182 EndY=-17.6395 EndZ=0
  constraints (16):
    c: Coincident(g0,g-5)
    c: Coincident(g0,g-5)
    c: Coincident(g1,g-3)
    c: PointOnObject(g1,g0)
    c: Perpendicular(g0,g1)
    c: PointOnObject(g2,g1)
    c: Parallel(g2,g0)
    c: Distance(g2,g1) = 4
    c: Distance(g2) = 38
    c: Coincident(g3,g2)
    c: PointOnObject(g3,g-4)
    c: Perpendicular(g3,g2)
    c: Coincident(g4,g3)
    c: Coincident(g4,g1)
    c: Coincident(g5,g4)
    c: Coincident(g5,g2)
FEATURE [PartDesign::Pocket] Pocket005
  BaseFeature = -> Fillet007
  Direction = (-1,2e-16,-3e-16)
  Length = 13
  Length2 = 13
  Profile = -> Sketch008
  ReferenceAxis = -> Sketch008 [N_Axis]
  Type = 4
  expr: Length = 24 mm / 2 + 1 mm
  expr: Length2 = 24 mm / 2 + 1 mm
FEATURE [Sketcher::SketchObject] Sketch009
  ExternalGeometry = -> [Pocket005]
  FullyConstrained = true
  MapMode = 5
  Placement = pos=(5.7e-15,-2.39663,-22.8024) rot=(-1,0,0;0.10472rad)
  Support = -> [Pocket005]
  sketch-geometry (17):
    g0: LineSegment StartX=149.925 StartY=-49.3922 StartZ=0 EndX=173.925 EndY=-49.3922 EndZ=0
    g1: LineSegment StartX=173.925 StartY=-49.3922 StartZ=0 EndX=173.925 EndY=-85.3922 EndZ=0
    g2: LineSegment StartX=173.925 StartY=-85.3922 StartZ=0 EndX=149.925 EndY=-85.3922 EndZ=0
    g3: LineSegment StartX=149.925 StartY=-85.3922 StartZ=0 EndX=149.925 EndY=-49.3922 EndZ=0
    g4: GeomPoint X=161.925 Y=-49.3922 Z=0
    g5: LineSegment StartX=174.925 StartY=-49.3922 StartZ=0 EndX=167.925 EndY=-49.3922 EndZ=0
    g6: LineSegment StartX=167.925 StartY=-49.3922 StartZ=0 EndX=167.925 EndY=-65.3922 EndZ=0
    g7: LineSegment StartX=167.925 StartY=-65.3922 StartZ=0 EndX=174.925 EndY=-65.3922 EndZ=0
    g8: LineSegment StartX=174.925 StartY=-65.3922 StartZ=0 EndX=174.925 EndY=-49.3922 EndZ=0
    g9: LineSegment StartX=174.925 StartY=-87.3922 StartZ=0 EndX=167.925 EndY=-87.3922 EndZ=0
    g10: LineSegment StartX=167.925 StartY=-87.3922 StartZ=0 EndX=167.925 EndY=-79.3922 EndZ=0
    g11: LineSegment StartX=167.925 StartY=-79.3922 StartZ=0 EndX=174.925 EndY=-79.3922 EndZ=0
    g12: LineSegment StartX=174.925 StartY=-79.3922 StartZ=0 EndX=174.925 EndY=-87.3922 EndZ=0
    g13: LineSegment StartX=148.925 StartY=-87.3922 StartZ=0 EndX=155.925 EndY=-87.3922 EndZ=0
    g14: LineSegment StartX=155.925 StartY=-87.3922 StartZ=0 EndX=155.925 EndY=-79.3922 EndZ=0
    g15: LineSegment StartX=155.925 StartY=-79.3922 StartZ=0 EndX=148.925 EndY=-79.3922 EndZ=0
    g16: LineSegment StartX=148.925 StartY=-79.3922 StartZ=0 EndX=148.925 EndY=-87.3922 EndZ=0
  constraints (45):
    c: Coincident(g0,g1)
    c: Coincident(g1,g2)
    c: Coincident(g2,g3)
    c: Coincident(g3,g0)
    c: Horizontal(g0)
    c: Horizontal(g2)
    c: Vertical(g1)
    c: Vertical(g3)
    c: DistanceX(g0,g0) = 24
    c: DistanceY(g1,g1) = 36
    c: Symmetric(g0,g0,g4)
    c: Symmetric(g-4,g-5,g4)
    c: Coincident(g5,g6)
    c: Coincident(g6,g7)
    c: Coincident(g7,g8)
    c: Coincident(g8,g5)
    c: Horizontal(g5)
    c: Horizontal(g7)
    c: Vertical(g6)
    c: Vertical(g8)
    c: Coincident(g5,g-5)
    c: DistanceX(g5,g0) = 6
    c: DistanceY(g6,g6) = 16
    c: Coincident(g9,g10)
    c: Coincident(g10,g11)
    c: Coincident(g11,g12)
    c: Coincident(g12,g9)
    c: Horizontal(g9)
    c: Horizontal(g11)
    c: Vertical(g10)
    c: Vertical(g12)
    c: Coincident(g9,g-6)
    c: DistanceY(g1,g10) = 6
    c: DistanceX(g10,g1) = 6
    c: Coincident(g13,g14)
    c: Coincident(g14,g15)
    c: Coincident(g15,g16)
    c: Coincident(g16,g13)
    c: Horizontal(g13)
    c: Horizontal(g15)
    c: Vertical(g14)
    c: Vertical(g16)
    c: Coincident(g13,g-6)
    c: DistanceY(g2,g14) = 6
    c: DistanceX(g2,g14) = 6
FEATURE [PartDesign::Pad] Pad005
  BaseFeature = -> Pocket005
  Direction = (-3e-16,0.104528,0.994522)
  Length = 0.4
  Length2 = 10
  Profile = -> Sketch009
  ReferenceAxis = -> Sketch009 [N_Axis]
  Type = 0
FEATURE [PartDesign::Fillet] Fillet008
  Base = -> Pad005 [Edge532,Edge534,Edge600,Edge551,Edge536,Edge538,Edge607,Edge540,Edge545,Edge543,Edge541,Edge610,Edge548]
  BaseFeature = -> Pad005
  Radius = 1
  SupportTransform = false
  UseAllEdges = false
FEATURE [Sketcher::SketchObject] Sketch010
  ExternalGeometry = -> [Fillet008]
  FullyConstrained = false
  MapMode = 5
  Placement = pos=(6.1e-15,-2.35482,-22.4046) rot=(-1,0,0;0.10472rad)
  Support = -> [Fillet008]
  sketch-geometry (9):
    g0: LineSegment StartX=152.925 StartY=-82.3922 StartZ=0 EndX=170.925 EndY=-82.3922 EndZ=0
    g1: LineSegment StartX=170.925 StartY=-82.3922 StartZ=0 EndX=170.925 EndY=-57.3922 EndZ=0
    g2: LineSegment StartX=170.925 StartY=-57.3922 StartZ=0 EndX=152.925 EndY=-57.3922 EndZ=0
    g3: LineSegment StartX=152.925 StartY=-57.3922 StartZ=0 EndX=152.925 EndY=-82.3922 EndZ=0
    g4: Circle CenterX=170.925 CenterY=-57.3922 CenterZ=0 NormalX=0 NormalY=0 NormalZ=1 AngleXU=0 Radius=1.7343
    g5: Circle CenterX=170.925 CenterY=-82.3922 CenterZ=0 NormalX=0 NormalY=0 NormalZ=1 AngleXU=0 Radius=1.55026
    g6: Circle CenterX=152.925 CenterY=-82.3922 CenterZ=0 NormalX=0 NormalY=0 NormalZ=1 AngleXU=0 Radius=1.339
    g7: Circle CenterX=170.925 CenterY=-52.3922 CenterZ=0 NormalX=0 NormalY=0 NormalZ=1 AngleXU=0 Radius=1.85738
    g8: Circle CenterX=170.925 CenterY=-62.3922 CenterZ=0 NormalX=0 NormalY=0 NormalZ=1 AngleXU=0 Radius=1.70469
  constraints (19):
    c: Coincident(g0,g1)
    c: Coincident(g1,g2)
    c: Coincident(g2,g3)
    c: Coincident(g3,g0)
    c: Horizontal(g0)
    c: Horizontal(g2)
    c: Vertical(g1)
    c: Vertical(g3)
    c: DistanceX(g0,g-4) = 3
    c: DistanceY(g0,g-3) = 3
    c: DistanceY(g3,g3) = 25
    c: DistanceX(g0,g0) = 18
    c: Coincident(g4,g1)
    c: Coincident(g5,g0)
    c: Coincident(g6,g3)
    c: PointOnObject(g8,g1)
    c: Vertical(g4,g7)
    c: DistanceY(g8,g4) = 5
    c: DistanceY(g4,g7) = 5
FEATURE [PartDesign::Hole] Hole
  BaseFeature = -> Fillet008
  CustomThreadClearance = 0
  Depth = 2.6
  DepthType = 0
  Diameter = 2.4
  DrillForDepth = false
  DrillPoint = 1
  DrillPointAngle = 118
  HoleCutCountersinkAngle = 90
  HoleCutCustomValues = false
  HoleCutDepth = 0
  HoleCutDiameter = 6.1
  HoleCutType = 0
  ModelThread = false
  Profile = -> Sketch010
  Tapered = false
  TaperedAngle = 90
  ThreadClass = 0
  ThreadDepth = 2.6
  ThreadDepthType = 0
  ThreadDirection = 0
  ThreadFit = 0
  ThreadSize = 6
  ThreadType = 1
  Threaded = false
  UseCustomThreadClearance = false
FEATURE [Sketcher::SketchObject] Sketch011
  ExternalGeometry = -> [Hole]
  FullyConstrained = true
  MapMode = 5
  Placement = pos=(-1.23e-14,-49.1216,5.16289) rot=(1,0,0;1.46608rad)
  Support = -> [Hole]
  expr: Constraints[13] = 8.94 mm + 0.1 mm
  sketch-geometry (15):
    g0: LineSegment StartX=149.925 StartY=-20.928 StartZ=0 EndX=173.925 EndY=-20.928 EndZ=0
    g1: LineSegment StartX=149.925 StartY=-17.668 StartZ=0 EndX=173.925 EndY=-17.668 EndZ=0
    g2: GeomPoint X=161.925 Y=-17.668 Z=0
    g3: LineSegment StartX=158.705 StartY=-17.668 StartZ=0 EndX=165.145 EndY=-17.668 EndZ=0
    g4: LineSegment StartX=166.445 StartY=-18.968 StartZ=0 EndX=166.445 EndY=-19.628 EndZ=0
    g5: LineSegment StartX=165.145 StartY=-20.928 StartZ=0 EndX=158.705 EndY=-20.928 EndZ=0
    g6: LineSegment StartX=157.405 StartY=-19.628 StartZ=0 EndX=157.405 EndY=-18.968 EndZ=0
    g7: ArcOfCircle CenterX=158.705 CenterY=-18.968 CenterZ=0 NormalX=0 NormalY=0 NormalZ=1 AngleXU=0 Radius=1.3 StartAngle=1.5708 EndAngle=3.14159
    g8: GeomPoint X=157.405 Y=-17.668 Z=0
    g9: ArcOfCircle CenterX=158.705 CenterY=-19.628 CenterZ=0 NormalX=0 NormalY=0 NormalZ=1 AngleXU=0 Radius=1.3 StartAngle=3.14159 EndAngle=4.71239
    g10: GeomPoint X=157.405 Y=-20.928 Z=0
    g11: ArcOfCircle CenterX=165.145 CenterY=-19.628 CenterZ=0 NormalX=0 NormalY=0 NormalZ=1 AngleXU=0 Radius=1.3 StartAngle=4.71239 EndAngle=6.28319
    g12: GeomPoint X=166.445 Y=-20.928 Z=0
    g13: ArcOfCircle CenterX=165.145 CenterY=-18.968 CenterZ=0 NormalX=0 NormalY=0 NormalZ=1 AngleXU=0 Radius=1.3 StartAngle=-1.8e-15 EndAngle=1.5708
    g14: GeomPoint X=166.445 Y=-17.668 Z=0
  constraints (36):
    c: PointOnObject(g0,g-4)
    c: PointOnObject(g0,g-5)
    c: Horizontal(g0)
    c: DistanceY(g-5,g0) = 1.6
    c: PointOnObject(g1,g-4)
    c: PointOnObject(g1,g-5)
    c: Horizontal(g1)
    c: DistanceY(g0,g1) = 3.26
    c: Symmetric(g1,g1,g2)
    c: Horizontal(g3)
    c: Horizontal(g5)
    c: Vertical(g4)
    c: Vertical(g6)
    c: DistanceX(g8,g14) = 9.04
    c: Symmetric(g8,g14,g2)
    c: PointOnObject(g10,g0)
    c: PointOnObject(g8,g6)
    c: PointOnObject(g8,g3)
    c: Tangent(g6,g7) = 1.5708
    c: Tangent(g3,g7) = 1.5708
    c: PointOnObject(g10,g6)
    c: PointOnObject(g10,g5)
    c: Tangent(g6,g9) = 1.5708
    c: Tangent(g5,g9) = 1.5708
    c: PointOnObject(g12,g5)
    c: PointOnObject(g12,g4)
    c: Tangent(g5,g11) = 1.5708
    c: Tangent(g4,g11) = 1.5708
    c: PointOnObject(g14,g3)
    c: PointOnObject(g14,g4)
    c: Tangent(g3,g13) = 1.5708
    c: Tangent(g4,g13) = 1.5708
    c: Radius(g7) = 1.3
    c: Equal(g7,g9)
    c: Equal(g7,g13)
    c: Equal(g11,g7)
FEATURE [PartDesign::Pocket] Pocket006
  BaseFeature = -> Hole
  Direction = (2e-16,0.994522,-0.104528)
  Length = 5
  Length2 = 5
  Profile = -> Sketch011
  ReferenceAxis = -> Sketch011 [N_Axis]
  Type = 1
FEATURE [Sketcher::SketchObject] Sketch012
  ExternalGeometry = -> [Pocket006]
  FullyConstrained = true
  MapMode = 5
  Placement = pos=(0.000358914,-39.7006,4.1727) rot=(-3e-06,0.743145,0.669131;3.1416rad)
  Support = -> [Pocket006]
  sketch-geometry (9):
    g0: LineSegment StartX=-173.925 StartY=-14.298 StartZ=0 EndX=-149.925 EndY=-14.298 EndZ=0
    g1: LineSegment StartX=-149.925 StartY=-14.298 StartZ=0 EndX=-149.925 EndY=-24.298 EndZ=0
    g2: LineSegment StartX=-149.925 StartY=-24.298 StartZ=0 EndX=-173.925 EndY=-24.298 EndZ=0
    g3: LineSegment StartX=-173.925 StartY=-24.298 StartZ=0 EndX=-173.925 EndY=-14.298 EndZ=0
    g4: GeomPoint X=-161.925 Y=-19.298 Z=0
    g5: LineSegment StartX=-173.925 StartY=-14.298 StartZ=0 EndX=-149.925 EndY=-14.298 EndZ=0
    g6: LineSegment StartX=-149.925 StartY=-14.298 StartZ=0 EndX=-149.925 EndY=-26.928 EndZ=0
    g7: LineSegment StartX=-149.925 StartY=-26.928 StartZ=0 EndX=-173.925 EndY=-26.928 EndZ=0
    g8: LineSegment StartX=-173.925 StartY=-26.928 StartZ=0 EndX=-173.925 EndY=-14.298 EndZ=0
  constraints (23):
    c: Coincident(g0,g1)
    c: Coincident(g1,g2)
    c: Coincident(g2,g3)
    c: Coincident(g3,g0)
    c: Horizontal(g0)
    c: Horizontal(g2)
    c: Vertical(g1)
    c: Vertical(g3)
    c: Symmetric(g-3,g-4,g4)
    c: DistanceX(g0,g0) = 24
    c: DistanceY(g3,g3) = 10
    c: Coincident(g5,g6)
    c: Coincident(g6,g7)
    c: Coincident(g7,g8)
    c: Coincident(g8,g5)
    c: Horizontal(g5)
    c: Horizontal(g7)
    c: Vertical(g6)
    c: Vertical(g8)
    c: Symmetric(g0,g1,g4)
    c: Coincident(g0,g5)
    c: PointOnObject(g6,g-5)
    c: Vertical(g1,g6)
FEATURE [PartDesign::Pocket] Pocket007
  BaseFeature = -> Pocket006
  Direction = (8.99101e-06,-0.994522,0.104528)
  Length = 6.47
  Length2 = 5
  Profile = -> Sketch012
  ReferenceAxis = -> Sketch012 [N_Axis]
  Type = 0
FEATURE [PartDesign::Fillet] Fillet009
  Base = -> Pocket007 [Edge641,Edge640]
  BaseFeature = -> Pocket007
  Radius = 4
  SupportTransform = false
  UseAllEdges = false
FEATURE [PartDesign::Chamfer] Chamfer002
  Angle = 45
  Base = -> Fillet009 [Edge6,Edge26,Edge29]
  BaseFeature = -> Fillet009
  ChamferType = 0
  FlipDirection = false
  Size = 2
  Size2 = 1
  SupportTransform = false
  UseAllEdges = false
FEATURE [Sketcher::SketchObject] Sketch013
  ExternalGeometry = -> [Chamfer002]
  FullyConstrained = true
  MapMode = 5
  Support = -> [Chamfer002]
  sketch-geometry (10):
    g0: Circle CenterX=30.491 CenterY=-30.576 CenterZ=0 NormalX=0 NormalY=0 NormalZ=1 AngleXU=0 Radius=1.5
    g1: Circle CenterX=153.925 CenterY=-45.3989 CenterZ=0 NormalX=0 NormalY=0 NormalZ=1 AngleXU=0 Radius=1.5
    g2: Circle CenterX=293.359 CenterY=-30.5756 CenterZ=0 NormalX=0 NormalY=0 NormalZ=1 AngleXU=0 Radius=1.5
    g3: Circle CenterX=58.491 CenterY=-102.775 CenterZ=0 NormalX=0 NormalY=0 NormalZ=1 AngleXU=0 Radius=1.5
    g4: Circle CenterX=169.925 CenterY=-45.3989 CenterZ=0 NormalX=0 NormalY=0 NormalZ=1 AngleXU=0 Radius=1.5
    g5: Circle CenterX=265.359 CenterY=-102.775 CenterZ=0 NormalX=0 NormalY=0 NormalZ=1 AngleXU=0 Radius=1.5
    g6: GeomPoint X=161.925 Y=-41.3989 Z=0
    g7: GeomPoint X=161.925 Y=-143.442 Z=0
    g8: Circle CenterX=145.925 CenterY=-135.442 CenterZ=0 NormalX=0 NormalY=0 NormalZ=1 AngleXU=0 Radius=1.5
    g9: Circle CenterX=177.925 CenterY=-135.442 CenterZ=0 NormalX=0 NormalY=0 NormalZ=1 AngleXU=0 Radius=1.5
  constraints (26):
    c: Diameter(g0) = 3
    c: Symmetric(g-7,g-7,g6)
    c: DistanceX(g1,g6) = 8
    c: DistanceX(g6,g4) = 8
    c: DistanceY(g1,g6) = 4
    c: Horizontal(g1,g4)
    c: Diameter(g1) = 3
    c: Equal(g1,g4)
    c: DistanceY(g0,g-3) = 8
    c: DistanceX(g-4,g0) = 8
    c: DistanceY(g-5,g3) = 8
    c: Equal(g0,g3)
    c: Symmetric(g-6,g-6,g7)
    c: DistanceX(g8,g7) = 16
    c: DistanceX(g7,g9) = 16
    c: DistanceY(g7,g8) = 8
    c: Horizontal(g8,g9)
    c: Diameter(g8) = 3
    c: Equal(g8,g9)
    c: Equal(g2,g0)
    c: DistanceY(g2,g-10) = 8
    c: DistanceX(g2,g-9) = 8
    c: DistanceX(g-4,g3) = 36
    c: Equal(g3,g5)
    c: DistanceY(g-8,g5) = 8
    c: DistanceX(g5,g-9) = 36
FEATURE [PartDesign::Pocket] Pocket008  label="Pocket008 - Magnet"
  BaseFeature = -> Chamfer002
  Direction = (0,0,-1)
  Length = 1.6
  Length2 = 5
  Profile = -> Sketch013
  ReferenceAxis = -> Sketch013 [N_Axis]
  Type = 0
FEATURE [Sketcher::SketchObject] Sketch014
  ExternalGeometry = -> [Fillet005]
  FullyConstrained = true
  MapMode = 5
  Placement = pos=(0,0,0) rot=(1,0,0;3.14159rad)
  Support = -> [Fillet005]
  sketch-geometry (10):
    g0: Circle CenterX=30.491 CenterY=30.576 CenterZ=0 NormalX=0 NormalY=0 NormalZ=1 AngleXU=0 Radius=1.5
    g1: Circle CenterX=293.359 CenterY=30.5756 CenterZ=0 NormalX=0 NormalY=0 NormalZ=1 AngleXU=0 Radius=1.5
    g2: Circle CenterX=265.359 CenterY=102.775 CenterZ=0 NormalX=0 NormalY=0 NormalZ=1 AngleXU=0 Radius=1.5
    g3: Circle CenterX=58.491 CenterY=102.775 CenterZ=0 NormalX=0 NormalY=0 NormalZ=1 AngleXU=0 Radius=1.5
    g4: Circle CenterX=145.925 CenterY=135.442 CenterZ=0 NormalX=0 NormalY=0 NormalZ=1 AngleXU=0 Radius=1.5
    g5: Circle CenterX=177.925 CenterY=135.442 CenterZ=0 NormalX=0 NormalY=0 NormalZ=1 AngleXU=0 Radius=1.5
    g6: Circle CenterX=153.925 CenterY=45.3989 CenterZ=0 NormalX=0 NormalY=0 NormalZ=1 AngleXU=0 Radius=1.5
    g7: Circle CenterX=169.925 CenterY=45.3989 CenterZ=0 NormalX=0 NormalY=0 NormalZ=1 AngleXU=0 Radius=1.5
    g8: GeomPoint X=161.925 Y=143.442 Z=0
    g9: GeomPoint X=161.925 Y=41.3989 Z=0
  constraints (26):
    c: DistanceY(g-10,g0) = 8
    c: DistanceX(g-3,g0) = 8
    c: Diameter(g0) = 3
    c: DistanceX(g-3,g3) = 36
    c: DistanceY(g3,g-9) = 8
    c: Equal(g0,g3)
    c: Equal(g0,g1)
    c: Equal(g0,g2)
    c: DistanceY(g2,g-8) = 8
    c: DistanceX(g2,g-6) = 36
    c: DistanceX(g1,g-6) = 8
    c: DistanceY(g-7,g1) = 8
    c: Symmetric(g-4,g-4,g9)
    c: Symmetric(g-5,g-5,g8)
    c: DistanceY(g9,g6) = 4
    c: DistanceX(g6,g9) = 8
    c: DistanceX(g9,g7) = 8
    c: Diameter(g6) = 3
    c: Equal(g6,g7)
    c: Horizontal(g6,g7)
    c: Horizontal(g4,g5)
    c: DistanceY(g4,g8) = 8
    c: DistanceX(g4,g8) = 16
    c: DistanceX(g8,g5) = 16
    c: Diameter(g4) = 3
    c: Equal(g4,g5)
FEATURE [PartDesign::Pocket] Pocket009  label="Pocket009 - Magnet"
  BaseFeature = -> Fillet005
  Direction = (0,0,1)
  Length = 1.6
  Length2 = 5
  Profile = -> Sketch014
  ReferenceAxis = -> Sketch014 [N_Axis]
  Type = 0
FEATURE [PartDesign::Body] Body001  label="Top"
  Group = -> [Sketch003,Pad001,Sketch004,Pocket002,Sketch005,Pocket003,Fillet003,Chamfer001,Fillet004,Fillet005,Sketch014,Pocket009]
  Origin = -> Origin001
  Tip = -> Pocket009
FEATURE [Sketcher::SketchObject] Sketch015
  AttachmentOffset = pos=(0,0,161.925) rot=(0,0,1;0rad)
  ExternalGeometry = -> [Pocket008]
  FullyConstrained = true
  MapMode = 5
  Placement = pos=(161.925,-3.6e-14,3.6e-14) rot=(0.57735,0.57735,0.57735;2.0944rad)
  Support = -> [YZ_Plane]
  expr: .AttachmentOffset.Base.z = 149.925 mm + 24 mm / 2
  sketch-geometry (3):
    g0: LineSegment StartX=-88.9246 StartY=-10 StartZ=0 EndX=-105.07 EndY=-10 EndZ=0
    g1: LineSegment StartX=-89.101 StartY=-11.6784 StartZ=0 EndX=-105.07 EndY=-10 EndZ=0
    g2: LineSegment StartX=-88.9246 StartY=-10 StartZ=0 EndX=-89.101 EndY=-11.6784 EndZ=0
  constraints (8):
    c: Coincident(g0,g-4)
    c: Parallel(g-5,g0)
    c: PointOnObject(g1,g-4)
    c: Parallel(g-3,g1)
    c: Distance(g-4,g1) = 1.6
    c: Coincident(g1,g0)
    c: Coincident(g2,g0)
    c: Coincident(g2,g1)
FEATURE [PartDesign::Pocket] Pocket010
  BaseFeature = -> Pocket008
  Direction = (-1,2e-16,-3e-16)
  Length = 5
  Length2 = 5
  Profile = -> Sketch015
  ReferenceAxis = -> Sketch015 [N_Axis]
  Type = 4
FEATURE [PartDesign::Fillet] Fillet010
  Base = -> Pocket010 [Edge808,Edge806]
  BaseFeature = -> Pocket010
  Radius = 1
  SupportTransform = false
  UseAllEdges = false
FEATURE [PartDesign::Body] Body  label="Bottom"
  Group = -> [Sketch,Pad,Sketch001,Pocket,Sketch002,Pocket001,Fillet,Pad004,Fillet001,Boolean,Sketch007,Pocket004,Chamfer,Fillet006,Fillet007,Sketch008,Pocket005,Sketch009,Pad005,Fillet008,Sketch010,Hole,Sketch011,Pocket006,Sketch012,Pocket007,Fillet009,Chamfer002,Sketch013,Pocket008,Sketch015,Pocket010,Fillet010]
  Origin = -> Origin
  Tip = -> Fillet010
FEATURE [Part::Feature] Part__Feature115  label="C_0402_1005Metric032"
  shape: bbox 1 x 0.5 x 0.5 mm, 28 faces (baked)
FEATURE [App::Part] C_0402_1005Metric016  label="C_0402_1005Metric033"
  Group = -> [Part__Feature115]
  Origin = -> Origin118
  Placement = pos=(4.22,6.655,1.65) rot=(0,0,1;1.5708rad)
FEATURE [Part::Feature] Part__Feature116  label="R_0402_1005Metric016"
  shape: bbox 1 x 0.5 x 0.35 mm, 26 faces (baked)
FEATURE [App::Part] R_0402_1005Metric008  label="R_0402_1005Metric017"
  Group = -> [Part__Feature116]
  Origin = -> Origin119
  Placement = pos=(-5.555,2.94,1.65) rot=(0,0,-1;1.5708rad)
FEATURE [Part::Feature] Part__Feature117  label="R_0402_1005Metric018"
  shape: bbox 1 x 0.5 x 0.35 mm, 26 faces (baked)
FEATURE [App::Part] R_0402_1005Metric009  label="R_0402_1005Metric019"
  Group = -> [Part__Feature117]
  Origin = -> Origin120
  Placement = pos=(2.22,6.655,1.65) rot=(0,0,1;1.5708rad)
FEATURE [Part::Feature] Part__Feature118  label="C_0402_1005Metric034"
  shape: bbox 1 x 0.5 x 0.5 mm, 28 faces (baked)
FEATURE [App::Part] C_0402_1005Metric017  label="C_0402_1005Metric035"
  Group = -> [Part__Feature118]
  Origin = -> Origin121
  Placement = pos=(1.58,-5.055,1.65) rot=(0,0,-1;1.5708rad)
FEATURE [Part::Feature] Part__Feature119  label="R_0402_1005Metric020"
  shape: bbox 1 x 0.5 x 0.35 mm, 26 faces (baked)
FEATURE [App::Part] R_0402_1005Metric010  label="R_0402_1005Metric021"
  Group = -> [Part__Feature119]
  Origin = -> Origin122
  Placement = pos=(-0.42,-5.595,1.65) rot=(0,0,-1;1.5708rad)
FEATURE [Part::Feature] Part__Feature120  label="C_0402_1005Metric036"
  shape: bbox 1 x 0.5 x 0.5 mm, 28 faces (baked)
FEATURE [App::Part] C_0402_1005Metric018  label="C_0402_1005Metric037"
  Group = -> [Part__Feature120]
  Origin = -> Origin123
  Placement = pos=(-6.16,-3.385,1.65) rot=(0,0,1;3.14159rad)
FEATURE [Part::Feature] Part__Feature121  label="R_0402_1005Metric022"
  shape: bbox 1 x 0.5 x 0.35 mm, 26 faces (baked)
FEATURE [App::Part] R_0402_1005Metric011  label="R_0402_1005Metric023"
  Group = -> [Part__Feature121]
  Origin = -> Origin124
  Placement = pos=(-10.48,10.285,1.65) rot=(0,0,1;3.14159rad)
FEATURE [Part::Feature] Part__Feature122  label="C_0402_1005Metric038"
  shape: bbox 1 x 0.5 x 0.5 mm, 28 faces (baked)
FEATURE [App::Part] C_0402_1005Metric019  label="C_0402_1005Metric039"
  Group = -> [Part__Feature122]
  Origin = -> Origin125
  Placement = pos=(-7.325,14.895,1.65) rot=(0,0,1;3.14159rad)
FEATURE [Part::Feature] Part__Feature123  label="R_0402_1005Metric024"
  shape: bbox 1 x 0.5 x 0.35 mm, 26 faces (baked)
FEATURE [App::Part] R_0402_1005Metric012  label="R_0402_1005Metric025"
  Group = -> [Part__Feature123]
  Origin = -> Origin126
  Placement = pos=(2.58,-5.055,1.65) rot=(0,0,1;1.5708rad)
FEATURE [Part::Feature] Part__Feature124  label="Crystal_SMD_3225-4Pin_3.2x2.5mm002"
  shape: bbox 3.2 x 2.501 x 0.64 mm, 28 faces (baked)
FEATURE [App::Part] Crystal_SMD_3225_4Pin_3_2x2_5mm001  label="Crystal_SMD_3225-4Pin_3.2x2.5mm003"
  Group = -> [Part__Feature124]
  Origin = -> Origin127
  Placement = pos=(-3.1,-4.925,1.65) rot=(0,0,1;0rad)
FEATURE [Part::Feature] Part__Feature125  label="C_0402_1005Metric040"
  shape: bbox 1 x 0.5 x 0.5 mm, 28 faces (baked)
FEATURE [App::Part] C_0402_1005Metric020  label="C_0402_1005Metric041"
  Group = -> [Part__Feature125]
  Origin = -> Origin128
  Placement = pos=(-1.8,7.94627,1.65) rot=(0,0,1;1.5708rad)
FEATURE [Part::Feature] Part__Feature126  label="C_0402_1005Metric042"
  shape: bbox 1 x 0.5 x 0.5 mm, 28 faces (baked)
FEATURE [App::Part] C_0402_1005Metric021  label="C_0402_1005Metric043"
  Group = -> [Part__Feature126]
  Origin = -> Origin129
  Placement = pos=(-5.64,11.345,1.65) rot=(0,0,1;1.5708rad)
FEATURE [Part::Feature] Part__Feature127  label="C_0402_1005Metric044"
  shape: bbox 1 x 0.5 x 0.5 mm, 28 faces (baked)
FEATURE [App::Part] C_0402_1005Metric022  label="C_0402_1005Metric045"
  Group = -> [Part__Feature127]
  Origin = -> Origin130
  Placement = pos=(-0.8,7.94627,1.65) rot=(0,0,1;1.5708rad)
FEATURE [Part::Feature] Part__Feature128  label="Body004"
  shape: bbox 8.94 x 7.3 x 3.2 mm, 10 faces (baked)
FEATURE [App::Part] HRO_TYPE_C_31_M_12_Body001  label="HRO_TYPE-C-31-M-12-Body001"
  Group = -> [Part__Feature128]
  Origin = -> Origin131
  Placement = pos=(-3e-16,11.705,1.65) rot=(0,0,1;3.14159rad)
FEATURE [Part::Feature] Part__Feature129  label="C_0402_1005Metric046"
  shape: bbox 1 x 0.5 x 0.5 mm, 28 faces (baked)
FEATURE [App::Part] C_0402_1005Metric023  label="C_0402_1005Metric047"
  Group = -> [Part__Feature129]
  Origin = -> Origin132
  Placement = pos=(5.035,3.81,1.65) rot=(0,0,1;0rad)
FEATURE [Part::Feature] Part__Feature130  label="Body005"
  shape: bbox 12.4 x 5.4 x 2 mm, 6 faces (baked)
FEATURE [App::Part] JUSHUO_AFC01_S16FCC_00_Body002  label="JUSHUO_AFC01-S16FCC-00-Body002"
  Group = -> [Part__Feature130]
  Origin = -> Origin133
  Placement = pos=(0,-13.515,1.65) rot=(0,0,1;0rad)
FEATURE [Part::Feature] Part__Feature131  label="C_0402_1005Metric048"
  shape: bbox 1 x 0.5 x 0.5 mm, 28 faces (baked)
FEATURE [App::Part] C_0402_1005Metric024  label="C_0402_1005Metric049"
  Group = -> [Part__Feature131]
  Origin = -> Origin134
  Placement = pos=(5.985,-2.20726,1.65) rot=(0,0,-1;1.5708rad)
FEATURE [Part::Feature] Part__Feature132  label="C_0402_1005Metric050"
  shape: bbox 1 x 0.5 x 0.5 mm, 28 faces (baked)
FEATURE [App::Part] C_0402_1005Metric025  label="C_0402_1005Metric051"
  Group = -> [Part__Feature132]
  Origin = -> Origin135
  Placement = pos=(3.22,6.655,1.65) rot=(0,0,1;1.5708rad)
FEATURE [Part::Feature] Part__Feature133  label="C_0402_1005Metric052"
  shape: bbox 1 x 0.5 x 0.5 mm, 28 faces (baked)
FEATURE [App::Part] C_0402_1005Metric026  label="C_0402_1005Metric053"
  Group = -> [Part__Feature133]
  Origin = -> Origin136
  Placement = pos=(-4.555,2.94,1.65) rot=(0,0,-1;1.5708rad)
FEATURE [Part::Feature] Part__Feature134  label="R_0402_1005Metric026"
  shape: bbox 1 x 0.5 x 0.35 mm, 26 faces (baked)
FEATURE [App::Part] R_0402_1005Metric013  label="R_0402_1005Metric027"
  Group = -> [Part__Feature134]
  Origin = -> Origin137
  Placement = pos=(-2.74,9.865,1.65) rot=(0,0,1;3.14159rad)
FEATURE [Part::Feature] Part__Feature135  label="C_0402_1005Metric054"
  shape: bbox 1 x 0.5 x 0.5 mm, 28 faces (baked)
FEATURE [App::Part] C_0402_1005Metric027  label="C_0402_1005Metric055"
  Group = -> [Part__Feature135]
  Origin = -> Origin138
  Placement = pos=(0.58,-5.055,1.65) rot=(0,0,-1;1.5708rad)
FEATURE [Part::Feature] Part__Feature136  label="C_0402_1005Metric056"
  shape: bbox 1 x 0.5 x 0.5 mm, 28 faces (baked)
FEATURE [App::Part] C_0402_1005Metric028  label="C_0402_1005Metric057"
  Group = -> [Part__Feature136]
  Origin = -> Origin139
  Placement = pos=(0.2,7.94627,1.65) rot=(0,0,1;1.5708rad)
FEATURE [Part::Feature] Part__Feature137  label="C_0402_1005Metric058"
  shape: bbox 1 x 0.5 x 0.5 mm, 28 faces (baked)
FEATURE [App::Part] C_0402_1005Metric029  label="C_0402_1005Metric059"
  Group = -> [Part__Feature137]
  Origin = -> Origin140
  Placement = pos=(5.035,4.81,1.65) rot=(0,0,1;0rad)
FEATURE [Part::Feature] Part__Feature138  label="R_0402_1005Metric028"
  shape: bbox 1 x 0.5 x 0.35 mm, 26 faces (baked)
FEATURE [App::Part] R_0402_1005Metric014  label="R_0402_1005Metric029"
  Group = -> [Part__Feature138]
  Origin = -> Origin141
  Placement = pos=(1.22,6.655,1.65) rot=(0,0,1;1.5708rad)
FEATURE [Part::Feature] Part__Feature139  label="C_0402_1005Metric060"
  shape: bbox 1 x 0.5 x 0.5 mm, 28 faces (baked)
FEATURE [App::Part] C_0402_1005Metric030  label="C_0402_1005Metric061"
  Group = -> [Part__Feature139]
  Origin = -> Origin142
  Placement = pos=(-6.16,-5.775,1.65) rot=(0,0,1;3.14159rad)
FEATURE [Part::Feature] Part__Feature140  label="R_0402_1005Metric030"
  shape: bbox 1 x 0.5 x 0.35 mm, 26 faces (baked)
FEATURE [App::Part] R_0402_1005Metric015  label="R_0402_1005Metric031"
  Group = -> [Part__Feature140]
  Origin = -> Origin143
  Placement = pos=(2.74,9.865,1.65) rot=(0,0,1;0rad)
FEATURE [Part::Feature] Part__Feature141  label="C_0402_1005Metric062"
  shape: bbox 1 x 0.5 x 0.5 mm, 28 faces (baked)
FEATURE [App::Part] C_0402_1005Metric031  label="C_0402_1005Metric063"
  Group = -> [Part__Feature141]
  Origin = -> Origin144
  Placement = pos=(-4.555,0.62,1.65) rot=(0,0,1;1.5708rad)
FEATURE [Part::Feature] Part__Feature142  label="SOT_23_006"
  shape: bbox 2.8 x 2.9 x 1.55 mm, 109 faces (baked)
FEATURE [App::Part] SOT_23_006  label="SOT-23-006"
  Group = -> [Part__Feature142]
  Origin = -> Origin145
  Placement = pos=(-7.8,12.385,1.65) rot=(0,0,1;1.5708rad)
FEATURE [Part::Feature] Part__Feature143  label="mcu-16-pcb_PCB001"
  shape: bbox 24 x 36 x 1.6 mm, 38 faces (baked)
FEATURE [App::Part] mcu_16_pcb_002  label="mcu-16-pcb"
  Group = -> [C_0402_1005Metric016,R_0402_1005Metric008,R_0402_1005Metric009,C_0402_1005Metric017,R_0402_1005Metric010,C_0402_1005Metric018,R_0402_1005Metric011,C_0402_1005Metric019,R_0402_1005Metric012,Crystal_SMD_3225_4Pin_3_2x2_5mm001,C_0402_1005Metric020,C_0402_1005Metric021,C_0402_1005Metric022,HRO_TYPE_C_31_M_12_Body001,C_0402_1005Metric023,JUSHUO_AFC01_S16FCC_00_Body002,C_0402_1005Metric024,+12 more]
  Origin = -> Origin146
  Placement = pos=(161.93,-69.4,-15.35) rot=(-1,0,0;0.10472rad)
FEATURE [Part::Feature] Part__Feature144  label="Hot_Swap_Socket_CPG151101S095"
  shape: bbox 14.5 x 6.096 x 3.05 mm, 90 faces, 3 solids (baked)
FEATURE [App::Part] Hot_Swap_Socket_CPG151101S053  label="Hot_Swap_Socket_CPG151101S096"
  Group = -> [Part__Feature144]
  Origin = -> Origin147
  Placement = pos=(266.7,-42.8625,-0.05) rot=(0,1,0;3.14159rad)
FEATURE [Part::Feature] Part__Feature145  label="Hot_Swap_Socket_CPG151101S097"
  shape: bbox 14.5 x 6.096 x 3.05 mm, 90 faces, 3 solids (baked)
FEATURE [App::Part] Hot_Swap_Socket_CPG151101S054  label="Hot_Swap_Socket_CPG151101S098"
  Group = -> [Part__Feature145]
  Origin = -> Origin148
  Placement = pos=(190.28,-121.645,-0.05) rot=(-0.326467,0.945208,0;3.14159rad)
FEATURE [Part::Feature] Part__Feature146  label="Hot_Swap_Socket_CPG151101S099"
  shape: bbox 14.5 x 6.096 x 3.05 mm, 90 faces, 3 solids (baked)
FEATURE [App::Part] Hot_Swap_Socket_CPG151101S055  label="Hot_Swap_Socket_CPG151101S100"
  Group = -> [Part__Feature146]
  Origin = -> Origin149
  Placement = pos=(226.498,-81.9726,-0.05) rot=(-0.142128,0.989848,0;3.14159rad)
FEATURE [Part::Feature] Part__Feature147  label="Hot_Swap_Socket_CPG151101S101"
  shape: bbox 14.5 x 6.096 x 3.05 mm, 90 faces, 3 solids (baked)
FEATURE [App::Part] Hot_Swap_Socket_CPG151101S056  label="Hot_Swap_Socket_CPG151101S102"
  Group = -> [Part__Feature147]
  Origin = -> Origin150
  Placement = pos=(97.352,-81.9726,-0.05) rot=(0.142119,0.98985,0;3.14159rad)
FEATURE [Part::Feature] Part__Feature148  label="D_SOD_365"
  shape: bbox 2.5 x 1.25 x 1.1 mm, 67 faces (baked)
FEATURE [App::Part] D_SOD_365  label="D_SOD-365"
  Group = -> [Part__Feature148]
  Origin = -> Origin151
  Placement = pos=(70.4954,-32.8925,-0.05) rot=(-0.666793,0.745243,0;3.14159rad)
FEATURE [Part::Feature] Part__Feature149  label="Hot_Swap_Socket_CPG151101S103"
  shape: bbox 14.5 x 6.096 x 3.05 mm, 90 faces, 3 solids (baked)
FEATURE [App::Part] Hot_Swap_Socket_CPG151101S057  label="Hot_Swap_Socket_CPG151101S104"
  Group = -> [Part__Feature149]
  Origin = -> Origin152
  Placement = pos=(188.963,-55.6463,-0.05) rot=(-0.22017,0.975462,0;3.14159rad)
FEATURE [Part::Feature] Part__Feature150  label="Hot_Swap_Socket_CPG151101S105"
  shape: bbox 14.5 x 6.096 x 3.05 mm, 90 faces, 3 solids (baked)
FEATURE [App::Part] Hot_Swap_Socket_CPG151101S058  label="Hot_Swap_Socket_CPG151101S106"
  Group = -> [Part__Feature150]
  Origin = -> Origin153
  Placement = pos=(134.689,-76.9221,-0.05) rot=(0.247084,0.968994,0;3.14159rad)
FEATURE [Part::Feature] Part__Feature151  label="Hot_Swap_Socket_CPG151101S107"
  shape: bbox 14.5 x 6.096 x 3.05 mm, 90 faces, 3 solids (baked)
FEATURE [App::Part] Hot_Swap_Socket_CPG151101S059  label="Hot_Swap_Socket_CPG151101S108"
  Group = -> [Part__Feature151]
  Origin = -> Origin154
  Placement = pos=(116.385,-68.3737,-0.05) rot=(0.186155,0.98252,0;3.14159rad)
FEATURE [Part::Feature] Part__Feature152  label="Hot_Swap_Socket_CPG151101S109"
  shape: bbox 14.5 x 6.096 x 3.05 mm, 90 faces, 3 solids (baked)
FEATURE [App::Part] Hot_Swap_Socket_CPG151101S060  label="Hot_Swap_Socket_CPG151101S110"
  Group = -> [Part__Feature152]
  Origin = -> Origin155
  Placement = pos=(97.1599,-62.1709,-0.05) rot=(0.124511,0.992218,0;3.14159rad)
FEATURE [Part::Feature] Part__Feature153  label="D_SOD_366"
  shape: bbox 2.5 x 1.25 x 1.1 mm, 67 faces (baked)
FEATURE [App::Part] D_SOD_366  label="D_SOD-366"
  Group = -> [Part__Feature153]
  Origin = -> Origin156
  Placement = pos=(278.39,-46.8475,-0.05) rot=(0.707107,-0.707107,0;3.14159rad)
FEATURE [Part::Feature] Part__Feature154  label="D_SOD_367"
  shape: bbox 2.5 x 1.25 x 1.1 mm, 67 faces (baked)
FEATURE [App::Part] D_SOD_367  label="D_SOD-367"
  Group = -> [Part__Feature154]
  Origin = -> Origin157
  Placement = pos=(238.546,-53.8296,-0.05) rot=(0.749834,-0.661626,0;3.14159rad)
FEATURE [Part::Feature] Part__Feature155  label="D_SOD_368"
  shape: bbox 2.5 x 1.25 x 1.1 mm, 67 faces (baked)
FEATURE [App::Part] D_SOD_368  label="D_SOD-368"
  Group = -> [Part__Feature155]
  Origin = -> Origin158
  Placement = pos=(30.74,-65.8975,-0.05) rot=(0.707107,-0.707107,0;3.14159rad)
FEATURE [Part::Feature] Part__Feature156  label="Hot_Swap_Socket_CPG151101S111"
  shape: bbox 14.5 x 6.096 x 3.05 mm, 90 faces, 3 solids (baked)
FEATURE [App::Part] Hot_Swap_Socket_CPG151101S061  label="Hot_Swap_Socket_CPG151101S112"
  Group = -> [Part__Feature156]
  Origin = -> Origin159
  Placement = pos=(38.1,-71.4375,-0.05) rot=(0,1,0;3.14159rad)
FEATURE [Part::Feature] Part__Feature157  label="D_SOD_369"
  shape: bbox 2.5 x 1.25 x 1.1 mm, 67 faces (baked)
FEATURE [App::Part] D_SOD_369  label="D_SOD-369"
  Group = -> [Part__Feature157]
  Origin = -> Origin160
  Placement = pos=(49.79,-56.3725,-0.05) rot=(0.707107,-0.707107,0;3.14159rad)
FEATURE [Part::Feature] Part__Feature158  label="Hot_Swap_Socket_CPG151101S113"
  shape: bbox 14.5 x 6.096 x 3.05 mm, 90 faces, 3 solids (baked)
FEATURE [App::Part] Hot_Swap_Socket_CPG151101S062  label="Hot_Swap_Socket_CPG151101S114"
  Group = -> [Part__Feature158]
  Origin = -> Origin161
  Placement = pos=(266.7,-61.9125,-0.05) rot=(0,1,0;3.14159rad)
FEATURE [Part::Feature] Part__Feature159  label="Hot_Swap_Socket_CPG151101S115"
  shape: bbox 14.5 x 6.096 x 3.05 mm, 90 faces, 3 solids (baked)
FEATURE [App::Part] Hot_Swap_Socket_CPG151101S063  label="Hot_Swap_Socket_CPG151101S116"
  Group = -> [Part__Feature159]
  Origin = -> Origin162
  Placement = pos=(207.42,-89.0785,-0.05) rot=(-0.212289,0.977207,0;3.14159rad)
FEATURE [Part::Feature] Part__Feature160  label="D_SOD_370"
  shape: bbox 2.5 x 1.25 x 1.1 mm, 67 faces (baked)
FEATURE [App::Part] D_SOD_370  label="D_SOD-370"
  Group = -> [Part__Feature160]
  Origin = -> Origin163
  Placement = pos=(70.9593,-71.1206,-0.05) rot=(-0.654925,0.755693,0;3.14159rad)
FEATURE [Part::Feature] Part__Feature161  label="D_SOD_371"
  shape: bbox 2.5 x 1.25 x 1.1 mm, 67 faces (baked)
FEATURE [App::Part] D_SOD_371  label="D_SOD-371"
  Group = -> [Part__Feature161]
  Origin = -> Origin164
  Placement = pos=(91.3971,-54.984,-0.05) rot=(-0.613555,0.789652,0;3.14159rad)
FEATURE [Part::Feature] Part__Feature162  label="D_SOD_372"
  shape: bbox 2.5 x 1.25 x 1.1 mm, 67 faces (baked)
FEATURE [App::Part] D_SOD_372  label="D_SOD-372"
  Group = -> [Part__Feature162]
  Origin = -> Origin165
  Placement = pos=(130.62,-47.482,-0.05) rot=(-0.534065,0.845444,0;3.14159rad)
FEATURE [Part::Feature] Part__Feature163  label="Hot_Swap_Socket_CPG151101S117"
  shape: bbox 14.5 x 6.096 x 3.05 mm, 90 faces, 3 solids (baked)
FEATURE [App::Part] Hot_Swap_Socket_CPG151101S064  label="Hot_Swap_Socket_CPG151101S118"
  Group = -> [Part__Feature163]
  Origin = -> Origin166
  Placement = pos=(77.3119,-58.4101,-0.05) rot=(0.062364,0.998053,0;3.14159rad)
FEATURE [Part::Feature] Part__Feature164  label="Hot_Swap_Socket_CPG151101S119"
  shape: bbox 14.5 x 6.096 x 3.05 mm, 90 faces, 3 solids (baked)
FEATURE [App::Part] Hot_Swap_Socket_CPG151101S065  label="Hot_Swap_Socket_CPG151101S120"
  Group = -> [Part__Feature164]
  Origin = -> Origin167
  Placement = pos=(226.854,-42.5411,-0.05) rot=(-0.110766,0.993846,0;3.14159rad)
FEATURE [Part::Feature] Part__Feature165  label="Hot_Swap_Socket_CPG151101S121"
  shape: bbox 14.5 x 6.096 x 3.05 mm, 90 faces, 3 solids (baked)
FEATURE [App::Part] Hot_Swap_Socket_CPG151101S066  label="Hot_Swap_Socket_CPG151101S122"
  Group = -> [Part__Feature165]
  Origin = -> Origin168
  Placement = pos=(57.15,-61.9125,-0.05) rot=(0,1,0;3.14159rad)
FEATURE [Part::Feature] Part__Feature166  label="Hot_Swap_Socket_CPG151101S123"
  shape: bbox 14.5 x 6.096 x 3.05 mm, 90 faces, 3 solids (baked)
FEATURE [App::Part] Hot_Swap_Socket_CPG151101S067  label="Hot_Swap_Socket_CPG151101S124"
  Group = -> [Part__Feature166]
  Origin = -> Origin169
  Placement = pos=(207.544,-48.0412,-0.05) rot=(-0.165719,0.986173,0;3.14159rad)
FEATURE [Part::Feature] Part__Feature167  label="Hot_Swap_Socket_CPG151101S125"
  shape: bbox 14.5 x 6.096 x 3.05 mm, 90 faces, 3 solids (baked)
FEATURE [App::Part] Hot_Swap_Socket_CPG151101S068  label="Hot_Swap_Socket_CPG151101S126"
  Group = -> [Part__Feature167]
  Origin = -> Origin170
  Placement = pos=(189.161,-76.9221,-0.05) rot=(-0.247084,0.968994,0;3.14159rad)
FEATURE [Part::Feature] Part__Feature168  label="D_SOD_373"
  shape: bbox 2.5 x 1.25 x 1.1 mm, 67 faces (baked)
FEATURE [App::Part] D_SOD_373  label="D_SOD-373"
  Group = -> [Part__Feature168]
  Origin = -> Origin171
  Placement = pos=(92.4269,-94.3954,-0.05) rot=(-0.580312,0.814394,0;3.14159rad)
FEATURE [Part::Feature] Part__Feature169  label="D_SOD_374"
  shape: bbox 2.5 x 1.25 x 1.1 mm, 67 faces (baked)
FEATURE [App::Part] D_SOD_374  label="D_SOD-374"
  Group = -> [Part__Feature169]
  Origin = -> Origin172
  Placement = pos=(217.877,-78.7273,-0.05) rot=(0.800428,-0.599429,0;3.14159rad)
FEATURE [Part::Feature] Part__Feature170  label="Hot_Swap_Socket_CPG151101S127"
  shape: bbox 14.5 x 6.096 x 3.05 mm, 90 faces, 3 solids (baked)
FEATURE [App::Part] Hot_Swap_Socket_CPG151101S069  label="Hot_Swap_Socket_CPG151101S128"
  Group = -> [Part__Feature170]
  Origin = -> Origin173
  Placement = pos=(97.575,-102.035,-0.05) rot=(0.165512,0.986208,0;3.14159rad)
FEATURE [Part::Feature] Part__Feature171  label="D_SOD_375"
  shape: bbox 2.5 x 1.25 x 1.1 mm, 67 faces (baked)
FEATURE [App::Part] D_SOD_375  label="D_SOD-375"
  Group = -> [Part__Feature171]
  Origin = -> Origin174
  Placement = pos=(111.562,-60.5253,-0.05) rot=(-0.563101,0.826388,0;3.14159rad)
FEATURE [Part::Feature] Part__Feature172  label="Hot_Swap_Socket_CPG151101S129"
  shape: bbox 14.5 x 6.096 x 3.05 mm, 90 faces, 3 solids (baked)
FEATURE [App::Part] Hot_Swap_Socket_CPG151101S070  label="Hot_Swap_Socket_CPG151101S130"
  Group = -> [Part__Feature172]
  Origin = -> Origin175
  Placement = pos=(77.1965,-39.2137,-0.05) rot=(0.055473,0.99846,0;3.14159rad)
FEATURE [Part::Feature] Part__Feature173  label="D_SOD_376"
  shape: bbox 2.5 x 1.25 x 1.1 mm, 67 faces (baked)
FEATURE [App::Part] D_SOD_376  label="D_SOD-376"
  Group = -> [Part__Feature173]
  Origin = -> Origin176
  Placement = pos=(278.39,-65.8975,-0.05) rot=(0.707107,-0.707107,0;3.14159rad)
FEATURE [Part::Feature] Part__Feature174  label="D_SOD_377"
  shape: bbox 2.5 x 1.25 x 1.1 mm, 67 faces (baked)
FEATURE [App::Part] D_SOD_377  label="D_SOD-377"
  Group = -> [Part__Feature174]
  Origin = -> Origin177
  Placement = pos=(112.032,-80.9841,-0.05) rot=(-0.540872,0.841105,0;3.14159rad)
FEATURE [Part::Feature] Part__Feature175  label="Hot_Swap_Socket_CPG151101S131"
  shape: bbox 14.5 x 6.096 x 3.05 mm, 90 faces, 3 solids (baked)
FEATURE [App::Part] Hot_Swap_Socket_CPG151101S071  label="Hot_Swap_Socket_CPG151101S132"
  Group = -> [Part__Feature175]
  Origin = -> Origin178
  Placement = pos=(96.9962,-42.5411,-0.05) rot=(0.110766,0.993846,0;3.14159rad)
FEATURE [Part::Feature] Part__Feature176  label="D_SOD_378"
  shape: bbox 2.5 x 1.25 x 1.1 mm, 67 faces (baked)
FEATURE [App::Part] D_SOD_378  label="D_SOD-378"
  Group = -> [Part__Feature176]
  Origin = -> Origin179
  Placement = pos=(180.359,-98.1357,-0.05) rot=(0.877498,-0.47958,0;3.14159rad)
FEATURE [Part::Feature] Part__Feature177  label="D_SOD_379"
  shape: bbox 2.5 x 1.25 x 1.1 mm, 67 faces (baked)
FEATURE [App::Part] D_SOD_379  label="D_SOD-379"
  Group = -> [Part__Feature177]
  Origin = -> Origin180
  Placement = pos=(30.74,-84.9475,-0.05) rot=(0.707107,-0.707107,0;3.14159rad)
FEATURE [Part::Feature] Part__Feature178  label="Hot_Swap_Socket_CPG151101S133"
  shape: bbox 14.5 x 6.096 x 3.05 mm, 90 faces, 3 solids (baked)
FEATURE [App::Part] Hot_Swap_Socket_CPG151101S072  label="Hot_Swap_Socket_CPG151101S134"
  Group = -> [Part__Feature178]
  Origin = -> Origin181
  Placement = pos=(246.538,-58.4101,-0.05) rot=(-0.062372,0.998053,0;3.14159rad)
FEATURE [Part::Feature] Part__Feature179  label="D_SOD_380"
  shape: bbox 2.5 x 1.25 x 1.1 mm, 67 faces (baked)
FEATURE [App::Part] D_SOD_380  label="D_SOD-380"
  Group = -> [Part__Feature179]
  Origin = -> Origin182
  Placement = pos=(259.34,-75.4225,-0.05) rot=(0.707107,-0.707107,0;3.14159rad)
FEATURE [Part::Feature] Part__Feature180  label="Hot_Swap_Socket_CPG151101S135"
  shape: bbox 14.5 x 6.096 x 3.05 mm, 90 faces, 3 solids (baked)
FEATURE [App::Part] Hot_Swap_Socket_CPG151101S073  label="Hot_Swap_Socket_CPG151101S136"
  Group = -> [Part__Feature180]
  Origin = -> Origin183
  Placement = pos=(246.654,-39.2137,-0.05) rot=(-0.055464,0.998461,0;3.14159rad)
FEATURE [Part::Feature] Part__Feature181  label="D_SOD_381"
  shape: bbox 2.5 x 1.25 x 1.1 mm, 67 faces (baked)
FEATURE [App::Part] D_SOD_381  label="D_SOD-381"
  Group = -> [Part__Feature181]
  Origin = -> Origin184
  Placement = pos=(49.79,-75.4225,-0.05) rot=(0.707107,-0.707107,0;3.14159rad)
FEATURE [Part::Feature] Part__Feature182  label="D_SOD_382"
  shape: bbox 2.5 x 1.25 x 1.1 mm, 67 faces (baked)
FEATURE [App::Part] D_SOD_382  label="D_SOD-382"
  Group = -> [Part__Feature182]
  Origin = -> Origin185
  Placement = pos=(238.725,-34.523,-0.05) rot=(0.745237,-0.666799,0;3.14159rad)
FEATURE [Part::Feature] Part__Feature183  label="D_SOD_383"
  shape: bbox 2.5 x 1.25 x 1.1 mm, 67 faces (baked)
FEATURE [App::Part] D_SOD_383  label="D_SOD-383"
  Group = -> [Part__Feature183]
  Origin = -> Origin186
  Placement = pos=(91.0366,-35.5165,-0.05) rot=(-0.624425,0.781085,0;3.14159rad)
FEATURE [Part::Feature] Part__Feature184  label="Hot_Swap_Socket_CPG151101S137"
  shape: bbox 14.5 x 6.096 x 3.05 mm, 90 faces, 3 solids (baked)
FEATURE [App::Part] Hot_Swap_Socket_CPG151101S074  label="Hot_Swap_Socket_CPG151101S138"
  Group = -> [Part__Feature184]
  Origin = -> Origin187
  Placement = pos=(57.15,-80.9625,-0.05) rot=(0,1,0;3.14159rad)
FEATURE [Part::Feature] Part__Feature185  label="Hot_Swap_Socket_CPG151101S139"
  shape: bbox 14.5 x 6.096 x 3.05 mm, 90 faces, 3 solids (baked)
FEATURE [App::Part] Hot_Swap_Socket_CPG151101S075  label="Hot_Swap_Socket_CPG151101S140"
  Group = -> [Part__Feature185]
  Origin = -> Origin188
  Placement = pos=(285.75,-52.3875,-0.05) rot=(0,1,0;3.14159rad)
FEATURE [Part::Feature] Part__Feature186  label="D_SOD_384"
  shape: bbox 2.5 x 1.25 x 1.1 mm, 67 faces (baked)
FEATURE [App::Part] D_SOD_384  label="D_SOD-384"
  Group = -> [Part__Feature186]
  Origin = -> Origin189
  Placement = pos=(278.39,-84.9475,-0.05) rot=(0.707107,-0.707107,0;3.14159rad)
FEATURE [Part::Feature] Part__Feature187  label="D_SOD_385"
  shape: bbox 2.5 x 1.25 x 1.1 mm, 67 faces (baked)
FEATURE [App::Part] D_SOD_385  label="D_SOD-385"
  Group = -> [Part__Feature187]
  Origin = -> Origin190
  Placement = pos=(259.34,-37.3225,-0.05) rot=(0.707107,-0.707107,0;3.14159rad)
FEATURE [Part::Feature] Part__Feature188  label="D_SOD_386"
  shape: bbox 2.5 x 1.25 x 1.1 mm, 67 faces (baked)
FEATURE [App::Part] D_SOD_386  label="D_SOD-386"
  Group = -> [Part__Feature188]
  Origin = -> Origin191
  Placement = pos=(180.047,-75.5829,-0.05) rot=(0.859897,-0.510468,0;3.14159rad)
FEATURE [Part::Feature] Part__Feature189  label="D_SOD_387"
  shape: bbox 2.5 x 1.25 x 1.1 mm, 67 faces (baked)
FEATURE [App::Part] D_SOD_387  label="D_SOD-387"
  Group = -> [Part__Feature189]
  Origin = -> Origin192
  Placement = pos=(91.8481,-74.5855,-0.05) rot=(-0.599422,0.800433,0;3.14159rad)
FEATURE [Part::Feature] Part__Feature190  label="Hot_Swap_Socket_CPG151101S141"
  shape: bbox 14.5 x 6.096 x 3.05 mm, 90 faces, 3 solids (baked)
FEATURE [App::Part] Hot_Swap_Socket_CPG151101S076  label="Hot_Swap_Socket_CPG151101S142"
  Group = -> [Part__Feature190]
  Origin = -> Origin193
  Placement = pos=(116.306,-48.0412,-0.05) rot=(0.165728,0.986172,0;3.14159rad)
FEATURE [Part::Feature] Part__Feature191  label="Hot_Swap_Socket_CPG151101S143"
  shape: bbox 14.5 x 6.096 x 3.05 mm, 90 faces, 3 solids (baked)
FEATURE [App::Part] Hot_Swap_Socket_CPG151101S077  label="Hot_Swap_Socket_CPG151101S144"
  Group = -> [Part__Feature191]
  Origin = -> Origin194
  Placement = pos=(246.393,-77.6505,-0.05) rot=(-0.071245,0.997459,0;3.14159rad)
FEATURE [Part::Feature] Part__Feature192  label="D_SOD_388"
  shape: bbox 2.5 x 1.25 x 1.1 mm, 67 faces (baked)
FEATURE [App::Part] D_SOD_388  label="D_SOD-388"
  Group = -> [Part__Feature192]
  Origin = -> Origin195
  Placement = pos=(198.778,-45.2113,-0.05) rot=(0.814511,-0.580149,0;3.14159rad)
FEATURE [Part::Feature] Part__Feature193  label="D_SOD_389"
  shape: bbox 2.5 x 1.25 x 1.1 mm, 67 faces (baked)
FEATURE [App::Part] D_SOD_389  label="D_SOD-389"
  Group = -> [Part__Feature193]
  Origin = -> Origin196
  Placement = pos=(218.189,-58.6212,-0.05) rot=(0.789647,-0.613562,0;3.14159rad)
FEATURE [Part::Feature] Part__Feature194  label="D_SOD_390"
  shape: bbox 2.5 x 1.25 x 1.1 mm, 67 faces (baked)
FEATURE [App::Part] D_SOD_390  label="D_SOD-390"
  Group = -> [Part__Feature194]
  Origin = -> Origin197
  Placement = pos=(238.32,-73.2129,-0.05) rot=(0.755688,-0.654932,0;3.14159rad)
FEATURE [Part::Feature] Part__Feature195  label="Hot_Swap_Socket_CPG151101S145"
  shape: bbox 14.5 x 6.096 x 3.05 mm, 90 faces, 3 solids (baked)
FEATURE [App::Part] Hot_Swap_Socket_CPG151101S078  label="Hot_Swap_Socket_CPG151101S146"
  Group = -> [Part__Feature195]
  Origin = -> Origin198
  Placement = pos=(266.7,-80.9625,-0.05) rot=(0,1,0;3.14159rad)
FEATURE [Part::Feature] Part__Feature196  label="D_SOD_391"
  shape: bbox 2.5 x 1.25 x 1.1 mm, 67 faces (baked)
FEATURE [App::Part] D_SOD_391  label="D_SOD-391"
  Group = -> [Part__Feature196]
  Origin = -> Origin199
  Placement = pos=(130.88,-68.5341,-0.05) rot=(-0.51046,0.859901,0;3.14159rad)
FEATURE [Part::Feature] Part__Feature197  label="Hot_Swap_Socket_CPG151101S147"
  shape: bbox 14.5 x 6.096 x 3.05 mm, 90 faces, 3 solids (baked)
FEATURE [App::Part] Hot_Swap_Socket_CPG151101S079  label="Hot_Swap_Socket_CPG151101S148"
  Group = -> [Part__Feature197]
  Origin = -> Origin200
  Placement = pos=(285.75,-71.4375,-0.05) rot=(0,1,0;3.14159rad)
FEATURE [Part::Feature] Part__Feature198  label="D_SOD_392"
  shape: bbox 2.5 x 1.25 x 1.1 mm, 67 faces (baked)
FEATURE [App::Part] D_SOD_392  label="D_SOD-392"
  Group = -> [Part__Feature198]
  Origin = -> Origin201
  Placement = pos=(259.34,-56.3725,-0.05) rot=(0.707107,-0.707107,0;3.14159rad)
FEATURE [Part::Feature] Part__Feature199  label="D_SOD_393"
  shape: bbox 2.5 x 1.25 x 1.1 mm, 67 faces (baked)
FEATURE [App::Part] D_SOD_393  label="D_SOD-393"
  Group = -> [Part__Feature199]
  Origin = -> Origin202
  Placement = pos=(30.74,-46.8475,-0.05) rot=(0.707107,-0.707107,0;3.14159rad)
FEATURE [Part::Feature] Part__Feature200  label="D_SOD_394"
  shape: bbox 2.5 x 1.25 x 1.1 mm, 67 faces (baked)
FEATURE [App::Part] D_SOD_394  label="D_SOD-394"
  Group = -> [Part__Feature200]
  Origin = -> Origin203
  Placement = pos=(181.07,-121.828,-0.05) rot=(0.899211,-0.437516,0;3.14159rad)
FEATURE [Part::Feature] Part__Feature201  label="D_SOD_395"
  shape: bbox 2.5 x 1.25 x 1.1 mm, 67 faces (baked)
FEATURE [App::Part] D_SOD_395  label="D_SOD-395"
  Group = -> [Part__Feature201]
  Origin = -> Origin204
  Placement = pos=(179.937,-53.8048,-0.05) rot=(0.845439,-0.534072,0;3.14159rad)
FEATURE [Part::Feature] Part__Feature202  label="D_SOD_396"
  shape: bbox 2.5 x 1.25 x 1.1 mm, 67 faces (baked)
FEATURE [App::Part] D_SOD_396  label="D_SOD-396"
  Group = -> [Part__Feature202]
  Origin = -> Origin205
  Placement = pos=(131.198,-112.744,-0.05) rot=(-0.437508,0.899214,0;3.14159rad)
FEATURE [Part::Feature] Part__Feature203  label="Hot_Swap_Socket_CPG151101S149"
  shape: bbox 14.5 x 6.096 x 3.05 mm, 90 faces, 3 solids (baked)
FEATURE [App::Part] Hot_Swap_Socket_CPG151101S080  label="Hot_Swap_Socket_CPG151101S150"
  Group = -> [Part__Feature203]
  Origin = -> Origin206
  Placement = pos=(77.4571,-77.6505,-0.05) rot=(0.071245,0.997459,0;3.14159rad)
FEATURE [Part::Feature] Part__Feature204  label="Hot_Swap_Socket_CPG151101S151"
  shape: bbox 14.5 x 6.096 x 3.05 mm, 90 faces, 3 solids (baked)
FEATURE [App::Part] Hot_Swap_Socket_CPG151101S081  label="Hot_Swap_Socket_CPG151101S152"
  Group = -> [Part__Feature204]
  Origin = -> Origin207
  Placement = pos=(133.57,-121.645,-0.05) rot=(0.326467,0.945208,0;3.14159rad)
FEATURE [Part::Feature] Part__Feature205  label="Hot_Swap_Socket_CPG151101S153"
  shape: bbox 14.5 x 6.096 x 3.05 mm, 90 faces, 3 solids (baked)
FEATURE [App::Part] Hot_Swap_Socket_CPG151101S082  label="Hot_Swap_Socket_CPG151101S154"
  Group = -> [Part__Feature205]
  Origin = -> Origin208
  Placement = pos=(207.465,-68.3737,-0.05) rot=(-0.186164,0.982519,0;3.14159rad)
FEATURE [Part::Feature] Part__Feature206  label="D_SOD_397"
  shape: bbox 2.5 x 1.25 x 1.1 mm, 67 faces (baked)
FEATURE [App::Part] D_SOD_397  label="D_SOD-397"
  Group = -> [Part__Feature206]
  Origin = -> Origin209
  Placement = pos=(111.161,-40.3997,-0.05) rot=(-0.580142,0.814516,0;3.14159rad)
FEATURE [Part::Feature] Part__Feature207  label="D_SOD_398"
  shape: bbox 2.5 x 1.25 x 1.1 mm, 67 faces (baked)
FEATURE [App::Part] D_SOD_398  label="D_SOD-398"
  Group = -> [Part__Feature207]
  Origin = -> Origin210
  Placement = pos=(49.79,-37.3225,-0.05) rot=(0.707107,-0.707107,0;3.14159rad)
FEATURE [Part::Feature] Part__Feature208  label="D_SOD_399"
  shape: bbox 2.5 x 1.25 x 1.1 mm, 67 faces (baked)
FEATURE [App::Part] D_SOD_399  label="D_SOD-399"
  Group = -> [Part__Feature208]
  Origin = -> Origin211
  Placement = pos=(198.588,-65.9102,-0.05) rot=(0.826383,-0.563108,0;3.14159rad)
FEATURE [Part::Feature] Part__Feature209  label="Hot_Swap_Socket_CPG151101S155"
  shape: bbox 14.5 x 6.096 x 3.05 mm, 90 faces, 3 solids (baked)
FEATURE [App::Part] Hot_Swap_Socket_CPG151101S083  label="Hot_Swap_Socket_CPG151101S156"
  Group = -> [Part__Feature209]
  Origin = -> Origin212
  Placement = pos=(189.545,-98.8239,-0.05) rot=(-0.28137,0.959599,0;3.14159rad)
FEATURE [Part::Feature] Part__Feature210  label="Hot_Swap_Socket_CPG151101S157"
  shape: bbox 14.5 x 6.096 x 3.05 mm, 90 faces, 3 solids (baked)
FEATURE [App::Part] Hot_Swap_Socket_CPG151101S084  label="Hot_Swap_Socket_CPG151101S158"
  Group = -> [Part__Feature210]
  Origin = -> Origin213
  Placement = pos=(134.887,-55.6463,-0.05) rot=(0.22017,0.975462,0;3.14159rad)
FEATURE [Part::Feature] Part__Feature211  label="Hot_Swap_Socket_CPG151101S159"
  shape: bbox 14.5 x 6.096 x 3.05 mm, 90 faces, 3 solids (baked)
FEATURE [App::Part] Hot_Swap_Socket_CPG151101S085  label="Hot_Swap_Socket_CPG151101S160"
  Group = -> [Part__Feature211]
  Origin = -> Origin214
  Placement = pos=(38.1,-52.3875,-0.05) rot=(0,1,0;3.14159rad)
FEATURE [Part::Feature] Part__Feature212  label="Hot_Swap_Socket_CPG151101S161"
  shape: bbox 14.5 x 6.096 x 3.05 mm, 90 faces, 3 solids (baked)
FEATURE [App::Part] Hot_Swap_Socket_CPG151101S086  label="Hot_Swap_Socket_CPG151101S162"
  Group = -> [Part__Feature212]
  Origin = -> Origin215
  Placement = pos=(226.69,-62.1709,-0.05) rot=(-0.124511,0.992218,0;3.14159rad)
FEATURE [Part::Feature] Part__Feature213  label="Hot_Swap_Socket_CPG151101S163"
  shape: bbox 14.5 x 6.096 x 3.05 mm, 90 faces, 3 solids (baked)
FEATURE [App::Part] Hot_Swap_Socket_CPG151101S087  label="Hot_Swap_Socket_CPG151101S164"
  Group = -> [Part__Feature213]
  Origin = -> Origin216
  Placement = pos=(134.305,-98.8239,-0.05) rot=(0.28137,0.959599,0;3.14159rad)
FEATURE [Part::Feature] Part__Feature214  label="D_SOD_400"
  shape: bbox 2.5 x 1.25 x 1.1 mm, 67 faces (baked)
FEATURE [App::Part] D_SOD_400  label="D_SOD-400"
  Group = -> [Part__Feature214]
  Origin = -> Origin217
  Placement = pos=(198.347,-108.996,-0.05) rot=(0.859768,-0.510685,0;3.14159rad)
FEATURE [Part::Feature] Part__Feature215  label="Hot_Swap_Socket_CPG151101S165"
  shape: bbox 14.5 x 6.096 x 3.05 mm, 90 faces, 3 solids (baked)
FEATURE [App::Part] Hot_Swap_Socket_CPG151101S088  label="Hot_Swap_Socket_CPG151101S166"
  Group = -> [Part__Feature215]
  Origin = -> Origin218
  Placement = pos=(207.46,-110.34,-0.05) rot=(-0.246838,0.969057,0;3.14159rad)
FEATURE [Part::Feature] Part__Feature216  label="D_SOD_401"
  shape: bbox 2.5 x 1.25 x 1.1 mm, 67 faces (baked)
FEATURE [App::Part] D_SOD_401  label="D_SOD-401"
  Group = -> [Part__Feature216]
  Origin = -> Origin219
  Placement = pos=(218.455,-38.7575,-0.05) rot=(0.781079,-0.624432,0;3.14159rad)
FEATURE [Part::Feature] Part__Feature217  label="Hot_Swap_Socket_CPG151101S167"
  shape: bbox 14.5 x 6.096 x 3.05 mm, 90 faces, 3 solids (baked)
FEATURE [App::Part] Hot_Swap_Socket_CPG151101S089  label="Hot_Swap_Socket_CPG151101S168"
  Group = -> [Part__Feature217]
  Origin = -> Origin220
  Placement = pos=(38.1,-90.4875,-0.05) rot=(0,1,0;3.14159rad)
FEATURE [Part::Feature] Part__Feature218  label="Body006"
  shape: bbox 12.4 x 5.4 x 2 mm, 6 faces (baked)
FEATURE [App::Part] JUSHUO_AFC01_S16FCC_00_Body003  label="JUSHUO_AFC01-S16FCC-00-Body003"
  Group = -> [Part__Feature218]
  Origin = -> Origin221
  Placement = pos=(161.925,-110.49,-0.05) rot=(1,0,0;3.14159rad)
FEATURE [Part::Feature] Part__Feature219  label="D_SOD_402"
  shape: bbox 2.5 x 1.25 x 1.1 mm, 67 faces (baked)
FEATURE [App::Part] D_SOD_402  label="D_SOD-402"
  Group = -> [Part__Feature219]
  Origin = -> Origin222
  Placement = pos=(217.51,-99.2009,-0.05) rot=(0.814389,-0.580319,0;3.14159rad)
FEATURE [Part::Feature] Part__Feature220  label="Hot_Swap_Socket_CPG151101S169"
  shape: bbox 14.5 x 6.096 x 3.05 mm, 90 faces, 3 solids (baked)
FEATURE [App::Part] Hot_Swap_Socket_CPG151101S090  label="Hot_Swap_Socket_CPG151101S170"
  Group = -> [Part__Feature220]
  Origin = -> Origin223
  Placement = pos=(285.75,-90.4875,-0.05) rot=(0,1,0;3.14159rad)
FEATURE [Part::Feature] Part__Feature221  label="Hot_Swap_Socket_CPG151101S171"
  shape: bbox 14.5 x 6.096 x 3.05 mm, 90 faces, 3 solids (baked)
FEATURE [App::Part] Hot_Swap_Socket_CPG151101S091  label="Hot_Swap_Socket_CPG151101S172"
  Group = -> [Part__Feature221]
  Origin = -> Origin224
  Placement = pos=(116.39,-110.34,-0.05) rot=(0.246838,0.969057,0;3.14159rad)
FEATURE [Part::Feature] Part__Feature222  label="Hot_Swap_Socket_CPG151101S173"
  shape: bbox 14.5 x 6.096 x 3.05 mm, 90 faces, 3 solids (baked)
FEATURE [App::Part] Hot_Swap_Socket_CPG151101S092  label="Hot_Swap_Socket_CPG151101S174"
  Group = -> [Part__Feature222]
  Origin = -> Origin225
  Placement = pos=(226.275,-102.035,-0.05) rot=(-0.165512,0.986208,0;3.14159rad)
FEATURE [Part::Feature] Part__Feature223  label="D_SOD_403"
  shape: bbox 2.5 x 1.25 x 1.1 mm, 67 faces (baked)
FEATURE [App::Part] D_SOD_403  label="D_SOD-403"
  Group = -> [Part__Feature223]
  Origin = -> Origin226
  Placement = pos=(131.102,-90.1866,-0.05) rot=(-0.479573,0.877502,0;3.14159rad)
FEATURE [Part::Feature] Part__Feature224  label="D_SOD_404"
  shape: bbox 2.5 x 1.25 x 1.1 mm, 67 faces (baked)
FEATURE [App::Part] D_SOD_404  label="D_SOD-404"
  Group = -> [Part__Feature224]
  Origin = -> Origin227
  Placement = pos=(112.577,-101.954,-0.05) rot=(-0.510678,0.859772,0;3.14159rad)
FEATURE [Part::Feature] Part__Feature225  label="D_SOD_405"
  shape: bbox 2.5 x 1.25 x 1.1 mm, 67 faces (baked)
FEATURE [App::Part] D_SOD_405  label="D_SOD-405"
  Group = -> [Part__Feature225]
  Origin = -> Origin228
  Placement = pos=(70.699,-51.9968,-0.05) rot=(-0.661619,0.74984,0;3.14159rad)
FEATURE [Part::Feature] Part__Feature226  label="D_SOD_406"
  shape: bbox 2.5 x 1.25 x 1.1 mm, 67 faces (baked)
FEATURE [App::Part] D_SOD_406  label="D_SOD-406"
  Group = -> [Part__Feature226]
  Origin = -> Origin229
  Placement = pos=(198.424,-87.0915,-0.05) rot=(0.8411,-0.540879,0;3.14159rad)
FEATURE [Part::Feature] Part__Feature227  label="Hot_Swap_Socket_CPG151101S175"
  shape: bbox 14.5 x 6.096 x 3.05 mm, 90 faces, 3 solids (baked)
FEATURE [App::Part] Hot_Swap_Socket_CPG151101S093  label="Hot_Swap_Socket_CPG151101S176"
  Group = -> [Part__Feature227]
  Origin = -> Origin230
  Placement = pos=(116.43,-89.0785,-0.05) rot=(0.212289,0.977207,0;3.14159rad)
FEATURE [Part::Feature] Part__Feature228  label="Hot_Swap_Socket_CPG151101S177"
  shape: bbox 14.5 x 6.096 x 3.05 mm, 90 faces, 3 solids (baked)
FEATURE [App::Part] Hot_Swap_Socket_CPG151101S094  label="Hot_Swap_Socket_CPG151101S178"
  Group = -> [Part__Feature228]
  Origin = -> Origin231
  Placement = pos=(57.15,-42.8625,-0.05) rot=(0,1,0;3.14159rad)
FEATURE [Part::Feature] Part__Feature229  label="harmony-42-pcb_PCB001"
  shape: bbox 266.7 x 106.3 x 1.6 mm, 256 faces (baked)
FEATURE [App::Part] harmony_42_pcb_002  label="harmony-42-pcb"
  Group = -> [Hot_Swap_Socket_CPG151101S053,Hot_Swap_Socket_CPG151101S054,Hot_Swap_Socket_CPG151101S055,Hot_Swap_Socket_CPG151101S056,D_SOD_365,Hot_Swap_Socket_CPG151101S057,Hot_Swap_Socket_CPG151101S058,Hot_Swap_Socket_CPG151101S059,Hot_Swap_Socket_CPG151101S060,D_SOD_366,D_SOD_367,D_SOD_368,Hot_Swap_Socket_CPG151101S061,D_SOD_369,Hot_Swap_Socket_CPG151101S062,Hot_Swap_Socket_CPG151101S063,D_SOD_370,D_SOD_371,+68 more]
  Origin = -> Origin232
  Placement = pos=(0,0,-5.08) rot=(0,0,1;0rad)
FEATURE [TechDraw::DrawSVGTemplate] Template
  Height = 297
  Orientation = 1
  Template = /Applications/FreeCAD.app/Contents/Resources/share/Mod/TechDraw/Templates/A3_Landscape_EN_m52.svg
  Width = 420
FEATURE [TechDraw::DrawViewPart] View
  CoarseView = false
  Direction = (0,0,1)
  Focus = 100
  HardHidden = false
  IsoCount = 0
  IsoHidden = false
  IsoVisible = false
  LockPosition = false
  Perspective = false
  Rotation = 0
  ScaleType = 0
  ScrubCount = 0
  SeamHidden = false
  SeamVisible = false
  SmoothHidden = false
  SmoothVisible = true
  Source = -> [Body]
  X = 210
  XDirection = (1,0,0)
  Y = 148.368
FEATURE [TechDraw::DrawViewBalloon] Balloon
  BubbleShape = 1
  EndType = 0
  EndTypeScale = 1
  KinkLength = 5
  LockPosition = false
  OriginX = 9
  OriginY = 29.7421
  Rotation = 0
  ScaleType = 0
  ShapeScale = 1
  SourceView = -> View
  Text = M2 x 2.6mm
  TextWrapLen = -1
  X = 34
  Y = 54.74
FEATURE [TechDraw::DrawViewBalloon] Balloon001
  BubbleShape = 1
  EndType = 0
  EndTypeScale = 1
  KinkLength = 5
  LockPosition = false
  OriginX = 9
  OriginY = 24.7695
  Rotation = 0
  ScaleType = 0
  ShapeScale = 1
  SourceView = -> View
  Text = M2 x 2.6mm
  TextWrapLen = -1
  X = 39
  Y = 44.7695
FEATURE [TechDraw::DrawViewBalloon] Balloon002
  BubbleShape = 1
  EndType = 0
  EndTypeScale = 1
  KinkLength = 5
  LockPosition = false
  OriginX = 9
  OriginY = 19.7969
  Rotation = 0
  ScaleType = 0
  ShapeScale = 1
  SourceView = -> View
  Text = M2 x 2.6mm
  TextWrapLen = -1
  X = 44
  Y = 34.8
FEATURE [TechDraw::DrawViewBalloon] Balloon003
  BubbleShape = 1
  EndType = 0
  EndTypeScale = 1
  KinkLength = 5
  LockPosition = false
  OriginX = 9
  OriginY = -0.0935137
  Rotation = 0
  ScaleType = 0
  ShapeScale = 1
  SourceView = -> View
  Text = M2 x 2.6mm
  TextWrapLen = -1
  X = 49
  Y = 19.9065
FEATURE [TechDraw::DrawViewBalloon] Balloon004
  BubbleShape = 1
  EndType = 0
  EndTypeScale = 1
  KinkLength = 5
  LockPosition = false
  OriginX = -9
  OriginY = -0.0935137
  Rotation = 0
  ScaleType = 0
  ShapeScale = 1
  SourceView = -> View
  Text = M2 x 2.6mm
  TextWrapLen = -1
  X = -34
  Y = 19.9065
FEATURE [TechDraw::DrawPage] Page  label="Bottom - Page"
  KeepUpdated = true
  NextBalloonIndex = 6
  ProjectionType = 0
  Template = -> Template
  Views = -> [View,Balloon,Balloon001,Balloon002,Balloon003,Balloon004]
FEATURE [Part::Feature] Part__Feature  label="harmony-42-plate"
  Placement = pos=(0,0,-0.75) rot=(0,0,1;0rad)
  shape: bbox 272.7 x 113.6 x 1.5 mm, 422 faces (baked)
FEATURE [App::DocumentObjectGroup] Group  label="External Components"
  Group = -> [mcu_16_pcb_002,harmony_42_pcb_002,Part__Feature]
